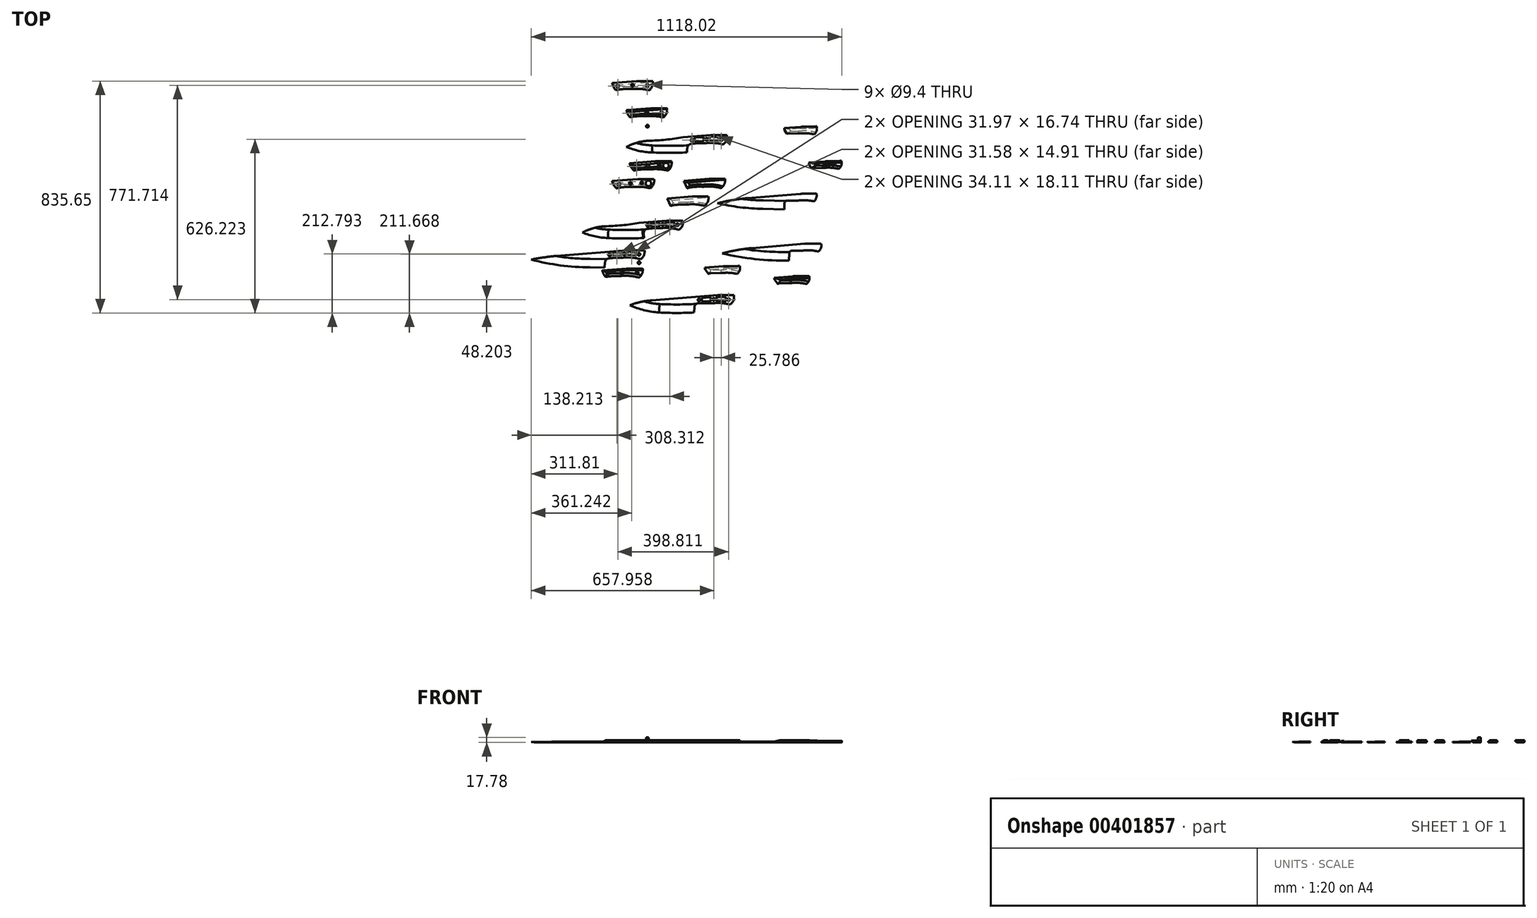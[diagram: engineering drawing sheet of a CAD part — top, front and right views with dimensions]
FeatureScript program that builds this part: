
annotation { "Feature Type Name" : "Feature", "Feature Type Description" : "" }
export const myFeature = defineFeature(function(context is Context, id is Id, definition is map)
    precondition{}
    {
        {
            var Q0;
            Q0=qCreatedBy(makeId("Top.planeOp"),FACE);
            var sketch = newSketch(context, id + "F0", { "sketchPlane" : qUnion([Q0])});
            skArc(sketch, "E0", {"start": v(-169.03, 335.4) * mm, "mid": v(-124.02, 321.28) * mm, "end": v(-77.2, 315.47) * mm});
            skArc(sketch, "E1", {"start": v(-77.2, 315.47) * mm, "mid": v(-14.27, 313.87) * mm, "end": v(48.66, 315.47) * mm});
            skArc(sketch, "E2", {"start": v(-90.69, 357.62) * mm, "mid": v(-131.02, 350.63) * mm, "end": v(-169.03, 335.4) * mm});
            skArc(sketch, "E3", {"start": v(-90.69, 357.62) * mm, "mid": v(-27.7, 361.34) * mm, "end": v(34.82, 369.92) * mm});
            skLineSegment(sketch, "E4", {"start": v(34.82, 369.92) * mm, "end": v(134.22, 377.8) * mm});
            skLineSegment(sketch, "E5", {"start": v(134.22, 377.8) * mm, "end": v(192.48, 377.8) * mm});
            skArc(sketch, "E6", {"start": v(179.14, 344.37) * mm, "mid": v(146.96, 349.5) * mm, "end": v(114.37, 348.8) * mm});
            skArc(sketch, "E7", {"start": v(179.14, 344.37) * mm, "mid": v(190.65, 359.16) * mm, "end": v(192.48, 377.8) * mm});
            skArc(sketch, "E8", {"start": v(114.37, 348.8) * mm, "mid": v(89.47, 349.08) * mm, "end": v(64.72, 346.26) * mm});
            skLineSegment(sketch, "E9", {"start": v(48.66, 315.47) * mm, "end": v(50.15, 331.6) * mm});
            skArc(sketch, "E10", {"start": v(64.72, 346.26) * mm, "mid": v(54.8, 341.55) * mm, "end": v(50.15, 331.6) * mm});
            skCircle(sketch, "E11", {"center": v(66.88, 359.7) * mm, "radius": 4.7 * mm});
            skCircle(sketch, "E12", {"center": v(173.1, 362.07) * mm, "radius": 4.7 * mm});
            skCircle(sketch, "E13", {"center": v(119.8, 363) * mm, "radius": 4.7 * mm});
            skArc(sketch, "E14", {"start": v(159.01, 354.25) * mm, "mid": v(146.32, 355.71) * mm, "end": v(133.55, 356) * mm});
            skArc(sketch, "E15", {"start": v(159.79, 371.2) * mm, "mid": v(146.02, 372.18) * mm, "end": v(132.22, 372.3) * mm});
            skArc(sketch, "E16", {"start": v(105.5, 355.53) * mm, "mid": v(93.56, 355.5) * mm, "end": v(81.67, 354.5) * mm});
            skLineSegment(sketch, "E17", {"start": v(79.5, 368.63) * mm, "end": v(104.68, 370.41) * mm});
            skArc(sketch, "E18", {"start": v(79.5, 368.63) * mm, "mid": v(77.02, 367.18) * mm, "end": v(76.66, 364.33) * mm});
            skArc(sketch, "E19", {"start": v(77.57, 358.02) * mm, "mid": v(78.79, 355.3) * mm, "end": v(81.67, 354.5) * mm});
            skArc(sketch, "E20", {"start": v(77.57, 358.02) * mm, "mid": v(77.6, 361.24) * mm, "end": v(76.66, 364.33) * mm});
            skArc(sketch, "E21", {"start": v(109.33, 365.54) * mm, "mid": v(108.15, 369.07) * mm, "end": v(104.68, 370.41) * mm});
            skArc(sketch, "E22", {"start": v(105.5, 355.53) * mm, "mid": v(108.55, 357.08) * mm, "end": v(109.33, 360.42) * mm});
            skArc(sketch, "E23", {"start": v(109.33, 365.54) * mm, "mid": v(109.01, 362.98) * mm, "end": v(109.33, 360.42) * mm});
            skArc(sketch, "E24", {"start": v(132.22, 372.3) * mm, "mid": v(129.65, 370.86) * mm, "end": v(129.4, 367.91) * mm});
            skArc(sketch, "E25", {"start": v(130.2, 360.09) * mm, "mid": v(130.86, 357.21) * mm, "end": v(133.55, 356) * mm});
            skArc(sketch, "E26", {"start": v(130.2, 360.09) * mm, "mid": v(130.55, 364.08) * mm, "end": v(129.4, 367.91) * mm});
            skArc(sketch, "E27", {"start": v(163.12, 366.2) * mm, "mid": v(162.63, 369.48) * mm, "end": v(159.79, 371.2) * mm});
            skArc(sketch, "E28", {"start": v(159.01, 354.25) * mm, "mid": v(162.07, 355.4) * mm, "end": v(162.9, 358.55) * mm});
            skArc(sketch, "E29", {"start": v(163.12, 366.2) * mm, "mid": v(162.3, 362.4) * mm, "end": v(162.9, 358.55) * mm});
            skSolve(sketch);
        }
        {
            var Q0;
            Q0=makeQuery(id+"F0.imprint","IMPRINT",FACE,{"disambiguationData":[TD([[makeQuery(id+"F0.imprint","IMPRINT",EDGE,{"derivedFrom":sQuery(id+"F0.wireOp",EDGE,"E0")}),1.0]])]});
            extrude(context, id + "F1", {"entities" : qUnion([Q0]), "depth" : 2.54 * mm});
        }
        {
            var Q0;
            Q0=qCreatedBy(makeId("Top.planeOp"),FACE);
            var sketch = newSketch(context, id + "F2", { "sketchPlane" : qUnion([Q0])});
            skArc(sketch, "E30", {"start": v(-175.57, 178.14) * mm, "mid": v(-130.56, 164.01) * mm, "end": v(-83.74, 158.2) * mm});
            skArc(sketch, "E31", {"start": v(-83.74, 158.2) * mm, "mid": v(-20.8, 156.6) * mm, "end": v(42.12, 158.2) * mm});
            skArc(sketch, "E32", {"start": v(-97.23, 200.35) * mm, "mid": v(-137.56, 193.36) * mm, "end": v(-175.57, 178.14) * mm});
            skArc(sketch, "E33", {"start": v(-97.23, 200.35) * mm, "mid": v(-34.23, 204.08) * mm, "end": v(28.29, 212.65) * mm});
            skLineSegment(sketch, "E34", {"start": v(28.29, 212.65) * mm, "end": v(127.68, 220.54) * mm});
            skLineSegment(sketch, "E35", {"start": v(127.68, 220.54) * mm, "end": v(185.94, 220.54) * mm});
            skArc(sketch, "E36", {"start": v(172.6, 187.1) * mm, "mid": v(140.42, 192.24) * mm, "end": v(107.83, 191.52) * mm});
            skArc(sketch, "E37", {"start": v(172.6, 187.1) * mm, "mid": v(184.11, 201.89) * mm, "end": v(185.94, 220.54) * mm});
            skArc(sketch, "E38", {"start": v(107.83, 191.52) * mm, "mid": v(82.93, 191.81) * mm, "end": v(58.18, 189) * mm});
            skLineSegment(sketch, "E39", {"start": v(42.12, 158.2) * mm, "end": v(43.61, 174.34) * mm});
            skArc(sketch, "E40", {"start": v(58.18, 189) * mm, "mid": v(48.26, 184.28) * mm, "end": v(43.61, 174.34) * mm});
            skLineSegment(sketch, "E41", {"start": v(37.58, 213.39) * mm, "end": v(50.38, 186.08) * mm});
            skLineSegment(sketch, "E42", {"start": v(58.18, 189) * mm, "end": v(49.42, 188.13) * mm});
            skSolve(sketch);
        }
        {
            var Q0;
            {var subQ0=sQuery(id+"F2.wireOp",EDGE,"E35");Q0=makeQuery(id+"F2.imprint","IMPRINT",FACE,{"disambiguationData":[TD([[makeQuery(id+"F2.imprint","IMPRINT",EDGE,{"derivedFrom":subQ0}),-1.0]])]});}
            var Q1;
            {var subQ0=sQuery(id+"F2.wireOp",EDGE,"E42");Q1=makeQuery(id+"F2.imprint","IMPRINT",FACE,{"disambiguationData":[TD([[makeQuery(id+"F2.imprint","IMPRINT",EDGE,{"derivedFrom":subQ0}),1.0]])]});}
            extrude(context, id + "F3", {"entities" : qUnion([Q0, Q1]), "depth" : 7.62 * mm, "offsetDistance" : 25.4 * mm});
        }
        {
            var Q0;
            Q0=makeQuery(id+"F3.opExtrude","CAP_EDGE",EDGE,{"disambiguationData":[OSD([sQuery(id+"F2.wireOp",EDGE,"E41")])],"isStart":false});
            chamfer(context, id + "F4", {"entities" : qUnion([Q0]), "chamferType" : ChamferType.TWO_OFFSETS, "width1" : 12.7 * mm, "oppositeDirection" : false, "width2" : 5.08 * mm, "tangentPropagation" : true});
        }
        {
            var Q0;
            Q0=makeQuery(id+"F1.opExtrude","CAP_EDGE",EDGE,{"disambiguationData":[OSD([sQuery(id+"F0.wireOp",EDGE,"E1")])],"isStart":false});
            var Q1;
            Q1=makeQuery(id+"F1.opExtrude","CAP_EDGE",EDGE,{"disambiguationData":[OSD([sQuery(id+"F0.wireOp",EDGE,"E0")])],"isStart":false});
            var Q2;
            Q2=makeQuery(id+"F1.opExtrude","CAP_EDGE",EDGE,{"disambiguationData":[OSD([sQuery(id+"F0.wireOp",EDGE,"E1")])],"isStart":true});
            var Q3;
            Q3=makeQuery(id+"F1.opExtrude","CAP_EDGE",EDGE,{"disambiguationData":[OSD([sQuery(id+"F0.wireOp",EDGE,"E0")])],"isStart":true});
            chamfer(context, id + "F5", {"entities" : qUnion([Q0, Q1, Q2, Q3]), "chamferType" : ChamferType.TWO_OFFSETS, "width1" : 25.4 * mm, "oppositeDirection" : false, "width2" : 1.02 * mm, "tangentPropagation" : true});
        }
        {
            var Q0;
            Q0=qCreatedBy(makeId("Top.planeOp"),FACE);
            var sketch = newSketch(context, id + "F6", { "sketchPlane" : qUnion([Q0])});
            skArc(sketch, "E43", {"start": v(-235.43, 114.12) * mm, "mid": v(-190.43, 100) * mm, "end": v(-143.61, 94.19) * mm});
            skArc(sketch, "E44", {"start": v(-143.61, 94.19) * mm, "mid": v(-80.68, 92.58) * mm, "end": v(-17.74, 94.19) * mm});
            skArc(sketch, "E45", {"start": v(-157.1, 136.34) * mm, "mid": v(-197.43, 129.34) * mm, "end": v(-235.43, 114.12) * mm});
            skArc(sketch, "E46", {"start": v(-157.1, 136.34) * mm, "mid": v(-94.1, 140.06) * mm, "end": v(-31.58, 148.64) * mm});
            skLineSegment(sketch, "E47", {"start": v(-31.58, 148.64) * mm, "end": v(67.8, 156.52) * mm});
            skLineSegment(sketch, "E48", {"start": v(67.8, 156.52) * mm, "end": v(126.07, 156.52) * mm});
            skArc(sketch, "E49", {"start": v(112.74, 123.09) * mm, "mid": v(80.55, 128.22) * mm, "end": v(47.97, 127.5) * mm});
            skArc(sketch, "E50", {"start": v(112.74, 123.09) * mm, "mid": v(124.24, 137.87) * mm, "end": v(126.07, 156.52) * mm});
            skArc(sketch, "E51", {"start": v(47.97, 127.5) * mm, "mid": v(23.06, 127.8) * mm, "end": v(-1.69, 124.98) * mm});
            skLineSegment(sketch, "E52", {"start": v(-17.74, 94.19) * mm, "end": v(-16.26, 110.32) * mm});
            skArc(sketch, "E53", {"start": v(-1.69, 124.98) * mm, "mid": v(-11.6, 120.27) * mm, "end": v(-16.26, 110.32) * mm});
            skLineSegment(sketch, "E54", {"start": v(-22.28, 149.37) * mm, "end": v(-9.49, 122.07) * mm});
            skLineSegment(sketch, "E55", {"start": v(-1.69, 124.98) * mm, "end": v(-10.45, 124.12) * mm});
            skSolve(sketch);
        }
        {
            var Q0;
            {var subQ0=sQuery(id+"F6.wireOp",EDGE,"E48");Q0=makeQuery(id+"F6.imprint","IMPRINT",FACE,{"disambiguationData":[TD([[makeQuery(id+"F6.imprint","IMPRINT",EDGE,{"derivedFrom":subQ0}),-1.0]])]});}
            var Q1;
            {var subQ0=sQuery(id+"F6.wireOp",EDGE,"E55");Q1=makeQuery(id+"F6.imprint","IMPRINT",FACE,{"disambiguationData":[TD([[makeQuery(id+"F6.imprint","IMPRINT",EDGE,{"derivedFrom":subQ0}),1.0]])]});}
            extrude(context, id + "F7", {"entities" : qUnion([Q0, Q1]), "depth" : 7.62 * mm, "offsetDistance" : 25.4 * mm});
        }
        {
            var Q0;
            Q0=makeQuery(id+"F7.opExtrude","CAP_EDGE",EDGE,{"disambiguationData":[OSD([sQuery(id+"F6.wireOp",EDGE,"E54")])],"isStart":true});
            chamfer(context, id + "F8", {"entities" : qUnion([Q0]), "chamferType" : ChamferType.TWO_OFFSETS, "width1" : 5.08 * mm, "oppositeDirection" : false, "width2" : 12.7 * mm, "tangentPropagation" : true});
        }
        {
            var Q0;
            Q0=makeQuery(id+"F7.opExtrude","CAP_EDGE",EDGE,{"disambiguationData":[OSD([sQuery(id+"F6.wireOp",EDGE,"E51")])],"isStart":true});
            var Q1;
            Q1=makeQuery(id+"F7.opExtrude","CAP_EDGE",EDGE,{"disambiguationData":[OSD([sQuery(id+"F6.wireOp",EDGE,"E47")])],"isStart":true});
            chamfer(context, id + "F9", {"entities" : qUnion([Q0, Q1]), "chamferType" : ChamferType.TWO_OFFSETS, "width1" : 7.62 * mm, "oppositeDirection" : false, "width2" : 5.08 * mm, "tangentPropagation" : true});
        }
        {
            var Q0;
            Q0=makeQuery(id+"F3.opExtrude","CAP_EDGE",EDGE,{"disambiguationData":[OSD([sQuery(id+"F2.wireOp",EDGE,"E34")])],"isStart":false});
            var Q1;
            Q1=makeQuery(id+"F3.opExtrude","CAP_EDGE",EDGE,{"disambiguationData":[OSD([sQuery(id+"F2.wireOp",EDGE,"E38")])],"isStart":false});
            chamfer(context, id + "F10", {"entities" : qUnion([Q0, Q1]), "chamferType" : ChamferType.TWO_OFFSETS, "width1" : 5.08 * mm, "oppositeDirection" : false, "width2" : 7.62 * mm, "tangentPropagation" : true});
        }
        {
            var Q0;
            Q0=makeQuery(id+"F3.opExtrude","CAP_EDGE",EDGE,{"disambiguationData":[OSD([sQuery(id+"F2.wireOp",EDGE,"E36")])],"isStart":false});
            var Q1;
            Q1=makeQuery(id+"F10.opChamfer","BLEND_EDGE",EDGE,{"blendedFrom":[makeQuery(id+"F3.opExtrude","CAP_EDGE",EDGE,{"disambiguationData":[OSD([sQuery(id+"F2.wireOp",EDGE,"E34")])],"isStart":false}),makeQuery(id+"F3.opExtrude","SWEPT_FACE",FACE,{"disambiguationData":[OSD([sQuery(id+"F2.wireOp",EDGE,"E35")])]})],"blendedInto":[makeQuery(id+"F3.opExtrude","SWEPT_FACE",FACE,{"disambiguationData":[OSD([sQuery(id+"F2.wireOp",EDGE,"E35")])]})]});
            chamfer(context, id + "F11", {"entities" : qUnion([Q0, Q1]), "chamferType" : ChamferType.TWO_OFFSETS, "width1" : 5.08 * mm, "oppositeDirection" : false, "width2" : 7.62 * mm, "tangentPropagation" : true});
        }
        {
            var Q0;
            Q0=makeQuery(id+"F7.opExtrude","CAP_EDGE",EDGE,{"disambiguationData":[OSD([sQuery(id+"F6.wireOp",EDGE,"E49")])],"isStart":true});
            chamfer(context, id + "F12", {"entities" : qUnion([Q0]), "chamferType" : ChamferType.TWO_OFFSETS, "width1" : 7.62 * mm, "oppositeDirection" : false, "width2" : 5.08 * mm, "tangentPropagation" : true});
        }
        {
            var Q0;
            Q0=qCreatedBy(makeId("Top.planeOp"),FACE);
            var sketch = newSketch(context, id + "F13", { "sketchPlane" : qUnion([Q0])});
            skArc(sketch, "E56", {"start": v(-367.85, 241) * mm, "mid": v(-322.84, 226.88) * mm, "end": v(-276.03, 221.07) * mm});
            skArc(sketch, "E57", {"start": v(-276.03, 221.07) * mm, "mid": v(-213.1, 219.46) * mm, "end": v(-150.16, 221.07) * mm});
            skArc(sketch, "E58", {"start": v(-289.51, 263.21) * mm, "mid": v(-329.85, 256.22) * mm, "end": v(-367.85, 241) * mm});
            skArc(sketch, "E59", {"start": v(-289.51, 263.21) * mm, "mid": v(-226.52, 266.94) * mm, "end": v(-164, 275.52) * mm});
            skLineSegment(sketch, "E60", {"start": v(-164, 275.52) * mm, "end": v(-64.6, 283.4) * mm});
            skLineSegment(sketch, "E61", {"start": v(-64.6, 283.4) * mm, "end": v(-6.35, 283.4) * mm});
            skArc(sketch, "E62", {"start": v(-19.68, 249.97) * mm, "mid": v(-51.87, 255.1) * mm, "end": v(-84.45, 254.39) * mm});
            skArc(sketch, "E63", {"start": v(-19.68, 249.97) * mm, "mid": v(-8.17, 264.75) * mm, "end": v(-6.35, 283.4) * mm});
            skArc(sketch, "E64", {"start": v(-84.45, 254.39) * mm, "mid": v(-109.36, 254.68) * mm, "end": v(-134.1, 251.86) * mm});
            skLineSegment(sketch, "E65", {"start": v(-150.16, 221.07) * mm, "end": v(-148.67, 237.2) * mm});
            skArc(sketch, "E66", {"start": v(-134.1, 251.86) * mm, "mid": v(-144.02, 247.15) * mm, "end": v(-148.67, 237.2) * mm});
            skCircle(sketch, "E67", {"center": v(-26.4, 268.03) * mm, "radius": 10.1 * mm});
            skCircle(sketch, "E68", {"center": v(-131.94, 265.3) * mm, "radius": 4.7 * mm});
            skCircle(sketch, "E69", {"center": v(-91.41, 267.64) * mm, "radius": 4.71 * mm});
            skCircle(sketch, "E70", {"center": v(-50.47, 269.22) * mm, "radius": 4.7 * mm});
            skLineSegment(sketch, "E71", {"start": v(-119.06, 273.98) * mm, "end": v(-106.19, 274.89) * mm});
            skLineSegment(sketch, "E72", {"start": v(-117.66, 260.1) * mm, "end": v(-105.57, 260.91) * mm});
            skLineSegment(sketch, "E73", {"start": v(-78.86, 277.2) * mm, "end": v(-63.77, 277.87) * mm});
            skLineSegment(sketch, "E74", {"start": v(-78.15, 261.02) * mm, "end": v(-63.57, 261.71) * mm});
            skArc(sketch, "E75", {"start": v(-78.86, 277.2) * mm, "mid": v(-81.33, 275.81) * mm, "end": v(-81.71, 273) * mm});
            skArc(sketch, "E76", {"start": v(-63.57, 261.71) * mm, "mid": v(-61.18, 263.02) * mm, "end": v(-60.72, 265.7) * mm});
            skArc(sketch, "E77", {"start": v(-60.38, 273.61) * mm, "mid": v(-61, 276.6) * mm, "end": v(-63.77, 277.87) * mm});
            skArc(sketch, "E78", {"start": v(-80.88, 265.13) * mm, "mid": v(-80.68, 262.3) * mm, "end": v(-78.15, 261.02) * mm});
            skArc(sketch, "E79", {"start": v(-80.88, 265.13) * mm, "mid": v(-80.55, 269.14) * mm, "end": v(-81.71, 273) * mm});
            skArc(sketch, "E80", {"start": v(-60.38, 273.61) * mm, "mid": v(-61.3, 269.69) * mm, "end": v(-60.72, 265.7) * mm});
            skArc(sketch, "E81", {"start": v(-119.06, 273.98) * mm, "mid": v(-121.72, 272.33) * mm, "end": v(-121.88, 269.2) * mm});
            skArc(sketch, "E82", {"start": v(-121.27, 263.7) * mm, "mid": v(-120.28, 261.09) * mm, "end": v(-117.66, 260.1) * mm});
            skArc(sketch, "E83", {"start": v(-101.85, 270.28) * mm, "mid": v(-102.93, 273.61) * mm, "end": v(-106.19, 274.89) * mm});
            skArc(sketch, "E84", {"start": v(-105.57, 260.91) * mm, "mid": v(-102.59, 262.6) * mm, "end": v(-102.06, 266) * mm});
            skArc(sketch, "E85", {"start": v(-101.85, 270.28) * mm, "mid": v(-102.21, 268.15) * mm, "end": v(-102.06, 266) * mm});
            skArc(sketch, "E86", {"start": v(-121.27, 263.7) * mm, "mid": v(-121.22, 266.5) * mm, "end": v(-121.88, 269.2) * mm});
            skArc(sketch, "E87", {"start": v(-157.02, 276.07) * mm, "mid": v(-151.1, 261.47) * mm, "end": v(-140.43, 249.87) * mm});
            skSolve(sketch);
        }
        {
            var Q0;
            {var subQ0=sQuery(id+"F13.wireOp",EDGE,"E61");Q0=makeQuery(id+"F13.imprint","IMPRINT",FACE,{"disambiguationData":[TD([[makeQuery(id+"F13.imprint","IMPRINT",EDGE,{"derivedFrom":subQ0}),-1.0]])]});}
            var Q1;
            Q1=makeQuery(id+"F13.imprint","IMPRINT",FACE,{"disambiguationData":[TD([[makeQuery(id+"F13.imprint","IMPRINT",EDGE,{"derivedFrom":sQuery(id+"F13.wireOp",EDGE,"E71")}),-1.0]])]});
            var Q2;
            Q2=makeQuery(id+"F13.imprint","IMPRINT",FACE,{"disambiguationData":[TD([[makeQuery(id+"F13.imprint","IMPRINT",EDGE,{"derivedFrom":sQuery(id+"F13.wireOp",EDGE,"E73")}),-1.0]])]});
            extrude(context, id + "F14", {"entities" : qUnion([Q0, Q1, Q2]), "depth" : 7.62 * mm, "offsetDistance" : 25.4 * mm});
        }
        {
            var Q0;
            Q0=qCreatedBy(makeId("Top.planeOp"),FACE);
            var sketch = newSketch(context, id + "F15", { "sketchPlane" : qUnion([Q0])});
            skArc(sketch, "E88", {"start": v(-431.18, 177.25) * mm, "mid": v(-386.18, 163.13) * mm, "end": v(-339.36, 157.32) * mm});
            skArc(sketch, "E89", {"start": v(-339.36, 157.32) * mm, "mid": v(-276.43, 155.71) * mm, "end": v(-213.5, 157.32) * mm});
            skArc(sketch, "E90", {"start": v(-352.84, 199.46) * mm, "mid": v(-393.18, 192.47) * mm, "end": v(-431.18, 177.25) * mm});
            skArc(sketch, "E91", {"start": v(-352.84, 199.46) * mm, "mid": v(-289.85, 203.19) * mm, "end": v(-227.33, 211.77) * mm});
            skLineSegment(sketch, "E92", {"start": v(-227.33, 211.77) * mm, "end": v(-127.94, 219.65) * mm});
            skLineSegment(sketch, "E93", {"start": v(-127.94, 219.65) * mm, "end": v(-69.68, 219.65) * mm});
            skArc(sketch, "E94", {"start": v(-83.01, 186.22) * mm, "mid": v(-115.2, 191.35) * mm, "end": v(-147.78, 190.64) * mm});
            skArc(sketch, "E95", {"start": v(-83.01, 186.22) * mm, "mid": v(-71.5, 201) * mm, "end": v(-69.68, 219.65) * mm});
            skArc(sketch, "E96", {"start": v(-147.78, 190.64) * mm, "mid": v(-172.7, 190.93) * mm, "end": v(-197.44, 188.1) * mm});
            skLineSegment(sketch, "E97", {"start": v(-213.5, 157.32) * mm, "end": v(-212, 173.45) * mm});
            skArc(sketch, "E98", {"start": v(-197.44, 188.1) * mm, "mid": v(-207.36, 183.4) * mm, "end": v(-212, 173.45) * mm});
            skCircle(sketch, "E99", {"center": v(-89.73, 204.28) * mm, "radius": 10.1 * mm});
            skCircle(sketch, "E100", {"center": v(-195.27, 201.54) * mm, "radius": 4.7 * mm});
            skCircle(sketch, "E101", {"center": v(-154.75, 203.9) * mm, "radius": 4.71 * mm});
            skCircle(sketch, "E102", {"center": v(-113.8, 205.47) * mm, "radius": 4.7 * mm});
            skLineSegment(sketch, "E103", {"start": v(-182.4, 210.23) * mm, "end": v(-169.52, 211.14) * mm});
            skLineSegment(sketch, "E104", {"start": v(-181, 196.36) * mm, "end": v(-168.9, 197.16) * mm});
            skLineSegment(sketch, "E105", {"start": v(-142.19, 213.45) * mm, "end": v(-127.1, 214.12) * mm});
            skLineSegment(sketch, "E106", {"start": v(-141.49, 197.27) * mm, "end": v(-126.9, 197.97) * mm});
            skArc(sketch, "E107", {"start": v(-142.19, 213.45) * mm, "mid": v(-144.67, 212.07) * mm, "end": v(-145.05, 209.25) * mm});
            skArc(sketch, "E108", {"start": v(-126.9, 197.97) * mm, "mid": v(-124.52, 199.27) * mm, "end": v(-124.06, 201.95) * mm});
            skArc(sketch, "E109", {"start": v(-123.72, 209.86) * mm, "mid": v(-124.33, 212.85) * mm, "end": v(-127.1, 214.12) * mm});
            skArc(sketch, "E110", {"start": v(-144.2, 201.38) * mm, "mid": v(-144.02, 198.55) * mm, "end": v(-141.49, 197.27) * mm});
            skArc(sketch, "E111", {"start": v(-144.2, 201.38) * mm, "mid": v(-143.89, 205.4) * mm, "end": v(-145.05, 209.25) * mm});
            skArc(sketch, "E112", {"start": v(-123.72, 209.86) * mm, "mid": v(-124.64, 205.94) * mm, "end": v(-124.06, 201.95) * mm});
            skArc(sketch, "E113", {"start": v(-182.4, 210.23) * mm, "mid": v(-185.06, 208.58) * mm, "end": v(-185.21, 205.46) * mm});
            skArc(sketch, "E114", {"start": v(-184.6, 199.95) * mm, "mid": v(-183.61, 197.34) * mm, "end": v(-181, 196.36) * mm});
            skArc(sketch, "E115", {"start": v(-165.19, 206.53) * mm, "mid": v(-166.26, 209.86) * mm, "end": v(-169.52, 211.14) * mm});
            skArc(sketch, "E116", {"start": v(-168.9, 197.16) * mm, "mid": v(-165.92, 198.86) * mm, "end": v(-165.39, 202.25) * mm});
            skArc(sketch, "E117", {"start": v(-165.19, 206.53) * mm, "mid": v(-165.55, 204.4) * mm, "end": v(-165.39, 202.25) * mm});
            skArc(sketch, "E118", {"start": v(-184.6, 199.95) * mm, "mid": v(-184.55, 202.74) * mm, "end": v(-185.21, 205.46) * mm});
            skArc(sketch, "E119", {"start": v(-220.36, 212.32) * mm, "mid": v(-214.43, 197.72) * mm, "end": v(-203.77, 186.12) * mm});
            skSolve(sketch);
        }
        {
            var Q0;
            {var subQ0=sQuery(id+"F15.wireOp",EDGE,"E93");Q0=makeQuery(id+"F15.imprint","IMPRINT",FACE,{"disambiguationData":[TD([[makeQuery(id+"F15.imprint","IMPRINT",EDGE,{"derivedFrom":subQ0}),-1.0]])]});}
            var Q1;
            Q1=makeQuery(id+"F15.imprint","IMPRINT",FACE,{"disambiguationData":[TD([[makeQuery(id+"F15.imprint","IMPRINT",EDGE,{"derivedFrom":sQuery(id+"F15.wireOp",EDGE,"E103")}),-1.0]])]});
            var Q2;
            Q2=makeQuery(id+"F15.imprint","IMPRINT",FACE,{"disambiguationData":[TD([[makeQuery(id+"F15.imprint","IMPRINT",EDGE,{"derivedFrom":sQuery(id+"F15.wireOp",EDGE,"E105")}),-1.0]])]});
            extrude(context, id + "F16", {"entities" : qUnion([Q0, Q1, Q2]), "depth" : 7.62 * mm, "offsetDistance" : 25.4 * mm});
        }
        {
            var Q0;
            Q0=makeQuery(id+"F14.opExtrude","CAP_EDGE",EDGE,{"disambiguationData":[OSD([sQuery(id+"F13.wireOp",EDGE,"E87")])],"isStart":false});
            var Q1;
            Q1=makeQuery(id+"F14.opExtrude","CAP_EDGE",EDGE,{"disambiguationData":[OSD([sQuery(id+"F13.wireOp",EDGE,"E64")])],"isStart":false});
            var Q2;
            Q2=makeQuery(id+"F14.opExtrude","CAP_EDGE",EDGE,{"disambiguationData":[OSD([sQuery(id+"F13.wireOp",EDGE,"E60")])],"isStart":false});
            var Q3;
            Q3=makeQuery(id+"F14.opExtrude","CAP_EDGE",EDGE,{"disambiguationData":[OSD([sQuery(id+"F13.wireOp",EDGE,"E62")])],"isStart":false});
            chamfer(context, id + "F17", {"entities" : qUnion([Q0, Q1, Q2, Q3]), "chamferType" : ChamferType.TWO_OFFSETS, "width1" : 7.62 * mm, "oppositeDirection" : false, "width2" : 5.08 * mm, "tangentPropagation" : true});
        }
        {
            var Q0;
            Q0=makeQuery(id+"F16.opExtrude","CAP_EDGE",EDGE,{"disambiguationData":[OSD([sQuery(id+"F15.wireOp",EDGE,"E119")])],"isStart":true});
            var Q1;
            Q1=makeQuery(id+"F16.opExtrude","CAP_EDGE",EDGE,{"disambiguationData":[OSD([sQuery(id+"F15.wireOp",EDGE,"E92")])],"isStart":true});
            var Q2;
            Q2=makeQuery(id+"F16.opExtrude","CAP_EDGE",EDGE,{"disambiguationData":[OSD([sQuery(id+"F15.wireOp",EDGE,"E96")])],"isStart":true});
            var Q3;
            Q3=makeQuery(id+"F16.opExtrude","CAP_EDGE",EDGE,{"disambiguationData":[OSD([sQuery(id+"F15.wireOp",EDGE,"E94")])],"isStart":true});
            chamfer(context, id + "F18", {"entities" : qUnion([Q0, Q1, Q2, Q3]), "chamferType" : ChamferType.TWO_OFFSETS, "width1" : 5.08 * mm, "oppositeDirection" : false, "width2" : 7.62 * mm, "tangentPropagation" : true});
        }
        {
            var Q0;
            Q0=qCreatedBy(makeId("Top.planeOp"),FACE);
            var sketch = newSketch(context, id + "F19", { "sketchPlane" : qUnion([Q0])});
            skArc(sketch, "E120", {"start": v(-384.45, 432.43) * mm, "mid": v(-339.44, 418.3) * mm, "end": v(-292.63, 412.5) * mm});
            skArc(sketch, "E121", {"start": v(-292.63, 412.5) * mm, "mid": v(-229.7, 410.89) * mm, "end": v(-166.76, 412.5) * mm});
            skArc(sketch, "E122", {"start": v(-306.11, 454.64) * mm, "mid": v(-346.45, 447.65) * mm, "end": v(-384.45, 432.43) * mm});
            skArc(sketch, "E123", {"start": v(-306.11, 454.64) * mm, "mid": v(-243.12, 458.37) * mm, "end": v(-180.6, 466.94) * mm});
            skLineSegment(sketch, "E124", {"start": v(-180.6, 466.94) * mm, "end": v(-81.21, 474.83) * mm});
            skLineSegment(sketch, "E125", {"start": v(-81.21, 474.83) * mm, "end": v(-22.95, 474.83) * mm});
            skArc(sketch, "E126", {"start": v(-36.28, 441.4) * mm, "mid": v(-68.47, 446.53) * mm, "end": v(-101.05, 445.81) * mm});
            skArc(sketch, "E127", {"start": v(-36.28, 441.4) * mm, "mid": v(-24.78, 456.18) * mm, "end": v(-22.95, 474.83) * mm});
            skArc(sketch, "E128", {"start": v(-101.05, 445.81) * mm, "mid": v(-125.96, 446.1) * mm, "end": v(-150.7, 443.29) * mm});
            skLineSegment(sketch, "E129", {"start": v(-166.76, 412.5) * mm, "end": v(-165.27, 428.63) * mm});
            skArc(sketch, "E130", {"start": v(-150.7, 443.29) * mm, "mid": v(-160.63, 438.58) * mm, "end": v(-165.27, 428.63) * mm});
            skCircle(sketch, "E131", {"center": v(-148.54, 456.72) * mm, "radius": 4.7 * mm});
            skCircle(sketch, "E132", {"center": v(-42.33, 459.1) * mm, "radius": 4.7 * mm});
            skCircle(sketch, "E133", {"center": v(-95.62, 460.01) * mm, "radius": 4.7 * mm});
            skArc(sketch, "E134", {"start": v(-56.41, 451.28) * mm, "mid": v(-69.1, 452.74) * mm, "end": v(-81.87, 453.02) * mm});
            skArc(sketch, "E135", {"start": v(-55.64, 468.21) * mm, "mid": v(-69.4, 469.2) * mm, "end": v(-83.2, 469.33) * mm});
            skArc(sketch, "E136", {"start": v(-109.93, 452.55) * mm, "mid": v(-121.87, 452.53) * mm, "end": v(-133.76, 451.53) * mm});
            skLineSegment(sketch, "E137", {"start": v(-135.92, 465.66) * mm, "end": v(-110.74, 467.44) * mm});
            skArc(sketch, "E138", {"start": v(-135.92, 465.66) * mm, "mid": v(-138.4, 464.2) * mm, "end": v(-138.77, 461.35) * mm});
            skArc(sketch, "E139", {"start": v(-137.86, 455.05) * mm, "mid": v(-136.64, 452.32) * mm, "end": v(-133.76, 451.53) * mm});
            skArc(sketch, "E140", {"start": v(-137.86, 455.05) * mm, "mid": v(-137.83, 458.27) * mm, "end": v(-138.77, 461.35) * mm});
            skArc(sketch, "E141", {"start": v(-106.1, 462.56) * mm, "mid": v(-107.27, 466.1) * mm, "end": v(-110.74, 467.44) * mm});
            skArc(sketch, "E142", {"start": v(-109.93, 452.55) * mm, "mid": v(-106.87, 454.1) * mm, "end": v(-106.1, 457.44) * mm});
            skArc(sketch, "E143", {"start": v(-106.1, 462.56) * mm, "mid": v(-106.41, 460) * mm, "end": v(-106.1, 457.44) * mm});
            skArc(sketch, "E144", {"start": v(-83.2, 469.33) * mm, "mid": v(-85.78, 467.88) * mm, "end": v(-86.02, 464.94) * mm});
            skArc(sketch, "E145", {"start": v(-85.23, 457.11) * mm, "mid": v(-84.57, 454.23) * mm, "end": v(-81.87, 453.02) * mm});
            skArc(sketch, "E146", {"start": v(-85.23, 457.11) * mm, "mid": v(-84.87, 461.1) * mm, "end": v(-86.02, 464.94) * mm});
            skArc(sketch, "E147", {"start": v(-52.3, 463.21) * mm, "mid": v(-52.8, 466.5) * mm, "end": v(-55.64, 468.21) * mm});
            skArc(sketch, "E148", {"start": v(-56.41, 451.28) * mm, "mid": v(-53.35, 452.41) * mm, "end": v(-52.53, 455.57) * mm});
            skArc(sketch, "E149", {"start": v(-52.3, 463.21) * mm, "mid": v(-53.13, 459.41) * mm, "end": v(-52.53, 455.57) * mm});
            skArc(sketch, "E150", {"start": v(-168.44, 467.9) * mm, "mid": v(-164.2, 453.87) * mm, "end": v(-155.5, 442.05) * mm});
            skArc(sketch, "E151", {"start": v(-435.84, 530.34) * mm, "mid": v(-390.83, 516.2) * mm, "end": v(-344.02, 510.4) * mm});
            skArc(sketch, "E152", {"start": v(-344.02, 510.4) * mm, "mid": v(-281.08, 508.8) * mm, "end": v(-218.15, 510.4) * mm});
            skArc(sketch, "E153", {"start": v(-357.5, 552.55) * mm, "mid": v(-397.84, 545.55) * mm, "end": v(-435.84, 530.34) * mm});
            skArc(sketch, "E154", {"start": v(-357.5, 552.55) * mm, "mid": v(-294.5, 556.27) * mm, "end": v(-231.99, 564.85) * mm});
            skLineSegment(sketch, "E155", {"start": v(-231.99, 564.85) * mm, "end": v(-132.6, 572.73) * mm});
            skLineSegment(sketch, "E156", {"start": v(-132.6, 572.73) * mm, "end": v(-74.34, 572.73) * mm});
            skArc(sketch, "E157", {"start": v(-87.67, 539.3) * mm, "mid": v(-119.86, 544.43) * mm, "end": v(-152.44, 543.72) * mm});
            skArc(sketch, "E158", {"start": v(-87.67, 539.3) * mm, "mid": v(-76.16, 554.08) * mm, "end": v(-74.34, 572.73) * mm});
            skArc(sketch, "E159", {"start": v(-152.44, 543.72) * mm, "mid": v(-177.35, 544) * mm, "end": v(-202.1, 541.19) * mm});
            skLineSegment(sketch, "E160", {"start": v(-218.15, 510.4) * mm, "end": v(-216.66, 526.53) * mm});
            skArc(sketch, "E161", {"start": v(-202.1, 541.19) * mm, "mid": v(-212.01, 536.48) * mm, "end": v(-216.66, 526.53) * mm});
            skCircle(sketch, "E162", {"center": v(-199.93, 554.63) * mm, "radius": 4.7 * mm});
            skCircle(sketch, "E163", {"center": v(-93.72, 557) * mm, "radius": 4.7 * mm});
            skCircle(sketch, "E164", {"center": v(-147, 557.92) * mm, "radius": 4.7 * mm});
            skArc(sketch, "E165", {"start": v(-107.8, 549.18) * mm, "mid": v(-120.5, 550.64) * mm, "end": v(-133.26, 550.93) * mm});
            skArc(sketch, "E166", {"start": v(-107.03, 566.12) * mm, "mid": v(-120.8, 567.1) * mm, "end": v(-134.6, 567.23) * mm});
            skArc(sketch, "E167", {"start": v(-161.32, 550.45) * mm, "mid": v(-173.26, 550.43) * mm, "end": v(-185.15, 549.43) * mm});
            skLineSegment(sketch, "E168", {"start": v(-187.31, 563.56) * mm, "end": v(-162.13, 565.34) * mm});
            skArc(sketch, "E169", {"start": v(-187.31, 563.56) * mm, "mid": v(-189.8, 562.1) * mm, "end": v(-190.16, 559.25) * mm});
            skArc(sketch, "E170", {"start": v(-189.25, 552.95) * mm, "mid": v(-188.03, 550.23) * mm, "end": v(-185.15, 549.43) * mm});
            skArc(sketch, "E171", {"start": v(-189.25, 552.95) * mm, "mid": v(-189.22, 556.17) * mm, "end": v(-190.16, 559.25) * mm});
            skArc(sketch, "E172", {"start": v(-157.49, 560.46) * mm, "mid": v(-158.66, 564) * mm, "end": v(-162.13, 565.34) * mm});
            skArc(sketch, "E173", {"start": v(-161.32, 550.45) * mm, "mid": v(-158.26, 552) * mm, "end": v(-157.48, 555.34) * mm});
            skArc(sketch, "E174", {"start": v(-157.49, 560.46) * mm, "mid": v(-157.8, 557.9) * mm, "end": v(-157.48, 555.34) * mm});
            skArc(sketch, "E175", {"start": v(-134.6, 567.23) * mm, "mid": v(-137.17, 565.78) * mm, "end": v(-137.4, 562.84) * mm});
            skArc(sketch, "E176", {"start": v(-136.61, 555.01) * mm, "mid": v(-135.95, 552.14) * mm, "end": v(-133.26, 550.93) * mm});
            skArc(sketch, "E177", {"start": v(-136.61, 555.01) * mm, "mid": v(-136.26, 559) * mm, "end": v(-137.4, 562.84) * mm});
            skArc(sketch, "E178", {"start": v(-103.7, 561.12) * mm, "mid": v(-104.18, 564.4) * mm, "end": v(-107.03, 566.12) * mm});
            skArc(sketch, "E179", {"start": v(-107.8, 549.18) * mm, "mid": v(-104.74, 550.32) * mm, "end": v(-103.92, 553.48) * mm});
            skArc(sketch, "E180", {"start": v(-103.7, 561.12) * mm, "mid": v(-104.52, 557.32) * mm, "end": v(-103.92, 553.48) * mm});
            skArc(sketch, "E181", {"start": v(-219.83, 565.81) * mm, "mid": v(-215.58, 551.77) * mm, "end": v(-206.9, 539.96) * mm});
            skCircle(sketch, "E182", {"center": v(-93.23, 409.92) * mm, "radius": 4.7 * mm});
            skSolve(sketch);
        }
        {
            var Q0;
            {var subQ0=sQuery(id+"F19.wireOp",EDGE,"E125");Q0=makeQuery(id+"F19.imprint","IMPRINT",FACE,{"disambiguationData":[TD([[makeQuery(id+"F19.imprint","IMPRINT",EDGE,{"derivedFrom":subQ0}),-1.0]])]});}
            var Q1;
            Q1=makeQuery(id+"F19.imprint","IMPRINT",FACE,{"disambiguationData":[TD([[makeQuery(id+"F19.imprint","IMPRINT",EDGE,{"derivedFrom":sQuery(id+"F19.wireOp",EDGE,"E136")}),-1.0]])]});
            var Q2;
            Q2=makeQuery(id+"F19.imprint","IMPRINT",FACE,{"disambiguationData":[TD([[makeQuery(id+"F19.imprint","IMPRINT",EDGE,{"derivedFrom":sQuery(id+"F19.wireOp",EDGE,"E134")}),-1.0]])]});
            var Q3;
            {var subQ0=sQuery(id+"F19.wireOp",EDGE,"E156");Q3=makeQuery(id+"F19.imprint","IMPRINT",FACE,{"disambiguationData":[TD([[makeQuery(id+"F19.imprint","IMPRINT",EDGE,{"derivedFrom":subQ0}),-1.0]])]});}
            var Q4;
            Q4=makeQuery(id+"F19.imprint","IMPRINT",FACE,{"disambiguationData":[TD([[makeQuery(id+"F19.imprint","IMPRINT",EDGE,{"derivedFrom":sQuery(id+"F19.wireOp",EDGE,"E167")}),-1.0]])]});
            var Q5;
            Q5=makeQuery(id+"F19.imprint","IMPRINT",FACE,{"disambiguationData":[TD([[makeQuery(id+"F19.imprint","IMPRINT",EDGE,{"derivedFrom":sQuery(id+"F19.wireOp",EDGE,"E165")}),-1.0]])]});
            extrude(context, id + "F20", {"entities" : qUnion([Q0, Q1, Q2, Q3, Q4, Q5]), "depth" : 7.62 * mm, "offsetDistance" : 25.4 * mm});
        }
        {
            var Q0;
            Q0=makeQuery(id+"F20.opExtrude","CAP_EDGE",EDGE,{"disambiguationData":[OSD([sQuery(id+"F19.wireOp",EDGE,"E128")])],"isStart":false});
            var Q1;
            Q1=makeQuery(id+"F20.opExtrude","CAP_EDGE",EDGE,{"disambiguationData":[OSD([sQuery(id+"F19.wireOp",EDGE,"E126")])],"isStart":false});
            var Q2;
            Q2=makeQuery(id+"F20.opExtrude","CAP_EDGE",EDGE,{"disambiguationData":[OSD([sQuery(id+"F19.wireOp",EDGE,"E124")])],"isStart":false});
            chamfer(context, id + "F21", {"entities" : qUnion([Q0, Q1, Q2]), "chamferType" : ChamferType.TWO_OFFSETS, "width1" : 5.08 * mm, "oppositeDirection" : false, "width2" : 7.62 * mm, "tangentPropagation" : true});
        }
        {
            var Q0;
            Q0=makeQuery(id+"F20.opExtrude","CAP_EDGE",EDGE,{"disambiguationData":[OSD([sQuery(id+"F19.wireOp",EDGE,"E181")])],"isStart":true});
            var Q1;
            Q1=makeQuery(id+"F20.opExtrude","CAP_EDGE",EDGE,{"disambiguationData":[OSD([sQuery(id+"F19.wireOp",EDGE,"E155")])],"isStart":true});
            var Q2;
            Q2=makeQuery(id+"F20.opExtrude","CAP_EDGE",EDGE,{"disambiguationData":[OSD([sQuery(id+"F19.wireOp",EDGE,"E159")])],"isStart":true});
            var Q3;
            Q3=makeQuery(id+"F20.opExtrude","CAP_EDGE",EDGE,{"disambiguationData":[OSD([sQuery(id+"F19.wireOp",EDGE,"E157")])],"isStart":true});
            chamfer(context, id + "F22", {"entities" : qUnion([Q0, Q1, Q2, Q3]), "chamferType" : ChamferType.TWO_OFFSETS, "width1" : 5.08 * mm, "oppositeDirection" : false, "width2" : 7.62 * mm, "tangentPropagation" : true});
        }
        {
            var Q0;
            Q0=makeQuery(id+"F19.imprint","IMPRINT",FACE,{"disambiguationData":[TD([[makeQuery(id+"F19.imprint","IMPRINT",EDGE,{"derivedFrom":sQuery(id+"F19.wireOp",EDGE,"E182")}),1.0]])]});
            extrude(context, id + "F23", {"entities" : qUnion([Q0]), "depth" : 17.78 * mm, "offsetDistance" : 25.4 * mm});
        }
        {
            var Q0;
            Q0=makeQuery(id+"F20.opExtrude","CAP_EDGE",EDGE,{"disambiguationData":[OSD([sQuery(id+"F19.wireOp",EDGE,"E150")])],"isStart":false});
            chamfer(context, id + "F24", {"entities" : qUnion([Q0]), "chamferType" : ChamferType.TWO_OFFSETS, "width1" : 12.7 * mm, "oppositeDirection" : false, "width2" : 5.08 * mm, "tangentPropagation" : true});
        }
        {
            var Q0;
            Q0=qCreatedBy(makeId("Top.planeOp"),FACE);
            var sketch = newSketch(context, id + "F25", { "sketchPlane" : qUnion([Q0])});
            skArc(sketch, "E183", {"start": v(-327.26, 27.01) * mm, "mid": v(-282.25, 12.88) * mm, "end": v(-235.43, 7.07) * mm});
            skArc(sketch, "E184", {"start": v(-235.43, 7.07) * mm, "mid": v(-172.5, 5.47) * mm, "end": v(-109.56, 7.07) * mm});
            skArc(sketch, "E185", {"start": v(-248.92, 49.22) * mm, "mid": v(-289.25, 42.23) * mm, "end": v(-327.26, 27.01) * mm});
            skArc(sketch, "E186", {"start": v(-248.92, 49.22) * mm, "mid": v(-185.92, 52.95) * mm, "end": v(-123.4, 61.52) * mm});
            skLineSegment(sketch, "E187", {"start": v(-123.4, 61.52) * mm, "end": v(-24.01, 69.4) * mm});
            skLineSegment(sketch, "E188", {"start": v(-24.01, 69.4) * mm, "end": v(34.25, 69.4) * mm});
            skLineSegment(sketch, "E189", {"start": v(-107.81, 25.74) * mm, "end": v(-109.56, 7.07) * mm});
            skArc(sketch, "E190", {"start": v(-93.5, 40.4) * mm, "mid": v(-103.25, 35.6) * mm, "end": v(-107.81, 25.74) * mm});
            skCircle(sketch, "E191", {"center": v(-38.57, 55.85) * mm, "radius": 4.76 * mm});
            skCircle(sketch, "E192", {"center": v(14.6, 54.9) * mm, "radius": 4.76 * mm});
            skCircle(sketch, "E193", {"center": v(-91.45, 52.47) * mm, "radius": 4.76 * mm});
            skArc(sketch, "E194", {"start": v(-43.86, 42.92) * mm, "mid": v(-68.72, 42.49) * mm, "end": v(-93.5, 40.4) * mm});
            skArc(sketch, "E195", {"start": v(-0.83, 47.96) * mm, "mid": v(-12.27, 49.34) * mm, "end": v(-23.8, 49.28) * mm});
            skArc(sketch, "E196", {"start": v(0, 63.67) * mm, "mid": v(-12.52, 64.47) * mm, "end": v(-25.06, 64.65) * mm});
            skLineSegment(sketch, "E197", {"start": v(-76.37, 47.71) * mm, "end": v(-52.88, 48.44) * mm});
            skLineSegment(sketch, "E198", {"start": v(-78, 60.93) * mm, "end": v(-53.7, 62.62) * mm});
            skArc(sketch, "E199", {"start": v(-49.68, 58.3) * mm, "mid": v(-50.66, 61.42) * mm, "end": v(-53.7, 62.62) * mm});
            skArc(sketch, "E200", {"start": v(-52.88, 48.44) * mm, "mid": v(-50.23, 49.74) * mm, "end": v(-49.47, 52.59) * mm});
            skArc(sketch, "E201", {"start": v(-78, 60.93) * mm, "mid": v(-80.58, 59.32) * mm, "end": v(-80.67, 56.28) * mm});
            skArc(sketch, "E202", {"start": v(-80.08, 51.35) * mm, "mid": v(-79, 48.74) * mm, "end": v(-76.37, 47.71) * mm});
            skArc(sketch, "E203", {"start": v(-49.68, 58.3) * mm, "mid": v(-49.94, 55.43) * mm, "end": v(-49.47, 52.59) * mm});
            skArc(sketch, "E204", {"start": v(-80.08, 51.35) * mm, "mid": v(-80.13, 53.84) * mm, "end": v(-80.67, 56.28) * mm});
            skArc(sketch, "E205", {"start": v(-25.06, 64.65) * mm, "mid": v(-27.63, 63.28) * mm, "end": v(-28.14, 60.41) * mm});
            skArc(sketch, "E206", {"start": v(-27.43, 53.5) * mm, "mid": v(-26.64, 50.5) * mm, "end": v(-23.8, 49.28) * mm});
            skArc(sketch, "E207", {"start": v(-27.43, 53.5) * mm, "mid": v(-27.23, 57.01) * mm, "end": v(-28.14, 60.41) * mm});
            skArc(sketch, "E208", {"start": v(3.59, 58.3) * mm, "mid": v(2.95, 61.76) * mm, "end": v(0, 63.67) * mm});
            skArc(sketch, "E209", {"start": v(-0.83, 47.96) * mm, "mid": v(2.5, 49.14) * mm, "end": v(3.3, 52.59) * mm});
            skArc(sketch, "E210", {"start": v(3.59, 58.3) * mm, "mid": v(3.07, 55.47) * mm, "end": v(3.3, 52.59) * mm});
            skArc(sketch, "E211", {"start": v(20.37, 36.9) * mm, "mid": v(-11.46, 42.97) * mm, "end": v(-43.86, 42.92) * mm});
            skArc(sketch, "E212", {"start": v(20.37, 36.9) * mm, "mid": v(32.03, 51.14) * mm, "end": v(34.25, 69.4) * mm});
            skArc(sketch, "E213", {"start": v(-111.45, 62.47) * mm, "mid": v(-106.46, 49.93) * mm, "end": v(-98.73, 38.87) * mm});
            skArc(sketch, "E214", {"start": v(-98.73, 38.87) * mm, "mid": v(-104.61, 32.66) * mm, "end": v(-106.6, 24.34) * mm});
            skLineSegment(sketch, "E215", {"start": v(-106.6, 24.34) * mm, "end": v(-106.13, 7.13) * mm});
            skLineSegment(sketch, "E216", {"start": v(-106.13, 7.13) * mm, "end": v(-109.56, 7.07) * mm});
            skSolve(sketch);
        }
        {
            var Q0;
            Q0=makeQuery(id+"F25.imprint","IMPRINT",FACE,{"disambiguationData":[TD([[makeQuery(id+"F25.imprint","IMPRINT",EDGE,{"derivedFrom":sQuery(id+"F25.wireOp",EDGE,"E183")}),1.0]])]});
            var Q1;
            {var subQ3=sQuery(id+"F25.wireOp",EDGE,"E188");Q1=makeQuery(id+"F25.imprint","IMPRINT",FACE,{"disambiguationData":[TD([[makeQuery(id+"F25.imprint","IMPRINT",EDGE,{"derivedFrom":subQ3}),-1.0]])]});}
            var Q2;
            {var subQ2=sQuery(id+"F25.wireOp",EDGE,"E189");Q2=makeQuery(id+"F25.imprint","IMPRINT",FACE,{"disambiguationData":[TD([[makeQuery(id+"F25.imprint","IMPRINT",EDGE,{"derivedFrom":subQ2}),1.0]])]});}
            extrude(context, id + "F26", {"entities" : qUnion([Q0, Q1, Q2]), "depth" : 2.54 * mm, "offsetDistance" : 25.4 * mm});
        }
        {
            var Q0;
            Q0=qCreatedBy(makeId("Top.planeOp"),FACE);
            var sketch = newSketch(context, id + "F27", { "sketchPlane" : qUnion([Q0])});
            skLineSegment(sketch, "E217", {"start": v(-162.23, -37.01) * mm, "end": v(-103.96, -37.01) * mm});
            skLineSegment(sketch, "E218", {"start": v(-246.03, -80.68) * mm, "end": v(-247.78, -99.34) * mm});
            skArc(sketch, "E219", {"start": v(-231.72, -66.02) * mm, "mid": v(-241.47, -70.82) * mm, "end": v(-246.03, -80.68) * mm});
            skCircle(sketch, "E220", {"center": v(-176.78, -50.57) * mm, "radius": 4.76 * mm});
            skCircle(sketch, "E221", {"center": v(-123.61, -51.53) * mm, "radius": 4.76 * mm});
            skCircle(sketch, "E222", {"center": v(-229.66, -53.95) * mm, "radius": 4.76 * mm});
            skArc(sketch, "E223", {"start": v(-182.07, -63.5) * mm, "mid": v(-206.94, -63.93) * mm, "end": v(-231.72, -66.02) * mm});
            skArc(sketch, "E224", {"start": v(-139.04, -58.46) * mm, "mid": v(-150.48, -57.08) * mm, "end": v(-162.01, -57.14) * mm});
            skArc(sketch, "E225", {"start": v(-138.21, -42.75) * mm, "mid": v(-150.73, -41.95) * mm, "end": v(-163.27, -41.77) * mm});
            skLineSegment(sketch, "E226", {"start": v(-214.58, -58.7) * mm, "end": v(-191.1, -57.98) * mm});
            skLineSegment(sketch, "E227", {"start": v(-216.21, -45.5) * mm, "end": v(-191.91, -43.8) * mm});
            skArc(sketch, "E228", {"start": v(-187.9, -48.11) * mm, "mid": v(-188.87, -45) * mm, "end": v(-191.91, -43.8) * mm});
            skArc(sketch, "E229", {"start": v(-191.1, -57.98) * mm, "mid": v(-188.45, -56.68) * mm, "end": v(-187.68, -53.83) * mm});
            skArc(sketch, "E230", {"start": v(-216.21, -45.5) * mm, "mid": v(-218.79, -47.1) * mm, "end": v(-218.88, -50.14) * mm});
            skArc(sketch, "E231", {"start": v(-218.29, -55.07) * mm, "mid": v(-217.2, -57.68) * mm, "end": v(-214.58, -58.7) * mm});
            skArc(sketch, "E232", {"start": v(-187.9, -48.11) * mm, "mid": v(-188.15, -50.98) * mm, "end": v(-187.68, -53.83) * mm});
            skArc(sketch, "E233", {"start": v(-218.29, -55.07) * mm, "mid": v(-218.35, -52.58) * mm, "end": v(-218.88, -50.14) * mm});
            skArc(sketch, "E234", {"start": v(-163.27, -41.77) * mm, "mid": v(-165.85, -43.14) * mm, "end": v(-166.36, -46) * mm});
            skArc(sketch, "E235", {"start": v(-165.65, -52.93) * mm, "mid": v(-164.85, -55.91) * mm, "end": v(-162.01, -57.14) * mm});
            skArc(sketch, "E236", {"start": v(-165.65, -52.93) * mm, "mid": v(-165.44, -49.4) * mm, "end": v(-166.36, -46) * mm});
            skArc(sketch, "E237", {"start": v(-134.63, -48.11) * mm, "mid": v(-135.26, -44.66) * mm, "end": v(-138.21, -42.75) * mm});
            skArc(sketch, "E238", {"start": v(-139.04, -58.46) * mm, "mid": v(-135.7, -57.28) * mm, "end": v(-134.91, -53.83) * mm});
            skArc(sketch, "E239", {"start": v(-134.63, -48.11) * mm, "mid": v(-135.15, -50.95) * mm, "end": v(-134.91, -53.83) * mm});
            skArc(sketch, "E240", {"start": v(-117.84, -69.53) * mm, "mid": v(-149.67, -63.45) * mm, "end": v(-182.07, -63.5) * mm});
            skArc(sketch, "E241", {"start": v(-117.84, -69.53) * mm, "mid": v(-106.18, -55.28) * mm, "end": v(-103.96, -37.01) * mm});
            skArc(sketch, "E242", {"start": v(-249.66, -43.95) * mm, "mid": v(-244.67, -56.49) * mm, "end": v(-236.94, -67.55) * mm});
            skArc(sketch, "E243", {"start": v(-471.85, -145.4) * mm, "mid": v(-426.85, -159.53) * mm, "end": v(-380.03, -165.34) * mm});
            skArc(sketch, "E244", {"start": v(-380.03, -165.34) * mm, "mid": v(-317.1, -166.94) * mm, "end": v(-254.16, -165.34) * mm});
            skArc(sketch, "E245", {"start": v(-393.51, -123.19) * mm, "mid": v(-433.85, -130.18) * mm, "end": v(-471.85, -145.4) * mm});
            skArc(sketch, "E246", {"start": v(-393.51, -123.19) * mm, "mid": v(-330.52, -119.46) * mm, "end": v(-268, -110.89) * mm});
            skLineSegment(sketch, "E247", {"start": v(-268, -110.89) * mm, "end": v(-168.61, -103) * mm});
            skLineSegment(sketch, "E248", {"start": v(-168.61, -103) * mm, "end": v(-110.35, -103) * mm});
            skLineSegment(sketch, "E249", {"start": v(-252.41, -146.67) * mm, "end": v(-254.16, -165.34) * mm});
            skArc(sketch, "E250", {"start": v(-238.1, -132.02) * mm, "mid": v(-247.85, -136.81) * mm, "end": v(-252.41, -146.67) * mm});
            skCircle(sketch, "E251", {"center": v(-183.17, -116.57) * mm, "radius": 4.76 * mm});
            skCircle(sketch, "E252", {"center": v(-130, -117.52) * mm, "radius": 4.76 * mm});
            skCircle(sketch, "E253", {"center": v(-236.05, -119.94) * mm, "radius": 4.76 * mm});
            skArc(sketch, "E254", {"start": v(-188.45, -129.5) * mm, "mid": v(-213.32, -129.92) * mm, "end": v(-238.1, -132.02) * mm});
            skArc(sketch, "E255", {"start": v(-145.43, -124.46) * mm, "mid": v(-156.87, -123.07) * mm, "end": v(-168.4, -123.13) * mm});
            skArc(sketch, "E256", {"start": v(-144.6, -108.74) * mm, "mid": v(-157.12, -107.94) * mm, "end": v(-169.66, -107.77) * mm});
            skLineSegment(sketch, "E257", {"start": v(-220.97, -124.7) * mm, "end": v(-197.48, -123.98) * mm});
            skLineSegment(sketch, "E258", {"start": v(-222.6, -111.48) * mm, "end": v(-198.3, -109.8) * mm});
            skArc(sketch, "E259", {"start": v(-194.28, -114.1) * mm, "mid": v(-195.26, -110.99) * mm, "end": v(-198.3, -109.8) * mm});
            skArc(sketch, "E260", {"start": v(-197.48, -123.98) * mm, "mid": v(-194.83, -122.67) * mm, "end": v(-194.07, -119.82) * mm});
            skArc(sketch, "E261", {"start": v(-222.6, -111.48) * mm, "mid": v(-225.17, -113.1) * mm, "end": v(-225.27, -116.14) * mm});
            skArc(sketch, "E262", {"start": v(-224.67, -121.07) * mm, "mid": v(-223.6, -123.67) * mm, "end": v(-220.97, -124.7) * mm});
            skArc(sketch, "E263", {"start": v(-194.28, -114.1) * mm, "mid": v(-194.54, -116.98) * mm, "end": v(-194.07, -119.82) * mm});
            skArc(sketch, "E264", {"start": v(-224.67, -121.07) * mm, "mid": v(-224.73, -118.57) * mm, "end": v(-225.27, -116.14) * mm});
            skArc(sketch, "E265", {"start": v(-169.66, -107.77) * mm, "mid": v(-172.23, -109.13) * mm, "end": v(-172.74, -112) * mm});
            skArc(sketch, "E266", {"start": v(-172.03, -118.92) * mm, "mid": v(-171.24, -121.9) * mm, "end": v(-168.4, -123.13) * mm});
            skArc(sketch, "E267", {"start": v(-172.03, -118.92) * mm, "mid": v(-171.83, -115.4) * mm, "end": v(-172.74, -112) * mm});
            skArc(sketch, "E268", {"start": v(-141.01, -114.1) * mm, "mid": v(-141.65, -110.65) * mm, "end": v(-144.6, -108.74) * mm});
            skArc(sketch, "E269", {"start": v(-145.43, -124.46) * mm, "mid": v(-142.09, -123.27) * mm, "end": v(-141.3, -119.82) * mm});
            skArc(sketch, "E270", {"start": v(-141.01, -114.1) * mm, "mid": v(-141.53, -116.95) * mm, "end": v(-141.3, -119.82) * mm});
            skArc(sketch, "E271", {"start": v(-124.23, -135.52) * mm, "mid": v(-156.06, -129.44) * mm, "end": v(-188.45, -129.5) * mm});
            skArc(sketch, "E272", {"start": v(-124.23, -135.52) * mm, "mid": v(-112.57, -121.28) * mm, "end": v(-110.35, -103) * mm});
            skArc(sketch, "E273", {"start": v(-256.05, -109.94) * mm, "mid": v(-251.05, -122.48) * mm, "end": v(-243.32, -133.55) * mm});
            skCircle(sketch, "E274", {"center": v(-123.36, -81.85) * mm, "radius": 4.76 * mm});
            skLineSegment(sketch, "E275", {"start": v(-247.78, -99.34) * mm, "end": v(-299.94, -98.39) * mm});
            skLineSegment(sketch, "E276", {"start": v(-103.96, -37.01) * mm, "end": v(-166.73, -37.01) * mm});
            skLineSegment(sketch, "E277", {"start": v(-166.73, -37.01) * mm, "end": v(-421.36, -57.57) * mm});
            skArc(sketch, "E278", {"start": v(-511.74, -70.61) * mm, "mid": v(-406.74, -91.36) * mm, "end": v(-299.94, -98.39) * mm});
            skArc(sketch, "E279", {"start": v(-421.36, -57.57) * mm, "mid": v(-466.75, -62.67) * mm, "end": v(-511.74, -70.61) * mm});
            skSolve(sketch);
        }
        {
            var Q0;
            Q0=makeQuery(id+"F26.opExtrude","CAP_EDGE",EDGE,{"disambiguationData":[OSD([sQuery(id+"F25.wireOp",EDGE,"E183")])],"isStart":false});
            var Q1;
            Q1=makeQuery(id+"F26.opExtrude","CAP_EDGE",EDGE,{"disambiguationData":[OSD([sQuery(id+"F25.wireOp",EDGE,"E183")])],"isStart":true});
            chamfer(context, id + "F28", {"entities" : qUnion([Q0, Q1]), "chamferType" : ChamferType.TWO_OFFSETS, "width1" : 30.48 * mm, "oppositeDirection" : false, "width2" : 1.14 * mm, "tangentPropagation" : true});
        }
        {
            var Q0;
            Q0=makeQuery(id+"F27.imprint","IMPRINT",FACE,{"disambiguationData":[TD([[makeQuery(id+"F27.imprint","IMPRINT",EDGE,{"derivedFrom":sQuery(id+"F27.wireOp",EDGE,"E274")}),1.0]])]});
            extrude(context, id + "F29", {"entities" : qUnion([Q0]), "depth" : 5.08 * mm, "offsetDistance" : 25.4 * mm});
        }
        {
            var Q0;
            Q0=qCreatedBy(makeId("Top.planeOp"),FACE);
            var sketch = newSketch(context, id + "F30", { "sketchPlane" : qUnion([Q0])});
            skArc(sketch, "E280", {"start": v(-51.42, -261.32) * mm, "mid": v(11.52, -262.92) * mm, "end": v(74.45, -261.32) * mm});
            skLineSegment(sketch, "E281", {"start": v(160, -198.98) * mm, "end": v(218.26, -198.98) * mm});
            skArc(sketch, "E282", {"start": v(204.93, -232.42) * mm, "mid": v(172.74, -227.28) * mm, "end": v(140.16, -228) * mm});
            skArc(sketch, "E283", {"start": v(204.93, -232.42) * mm, "mid": v(216.44, -217.63) * mm, "end": v(218.26, -198.98) * mm});
            skLineSegment(sketch, "E284", {"start": v(74.45, -261.32) * mm, "end": v(75.94, -245.18) * mm});
            skCircle(sketch, "E285", {"center": v(198.88, -214.72) * mm, "radius": 4.7 * mm});
            skCircle(sketch, "E286", {"center": v(145.6, -213.8) * mm, "radius": 4.7 * mm});
            skArc(sketch, "E287", {"start": v(184.8, -222.53) * mm, "mid": v(172.1, -221.07) * mm, "end": v(159.34, -220.79) * mm});
            skArc(sketch, "E288", {"start": v(185.57, -205.6) * mm, "mid": v(171.8, -204.6) * mm, "end": v(158, -204.48) * mm});
            skLineSegment(sketch, "E289", {"start": v(105.29, -208.15) * mm, "end": v(130.47, -206.37) * mm});
            skArc(sketch, "E290", {"start": v(105.29, -208.15) * mm, "mid": v(102.8, -209.6) * mm, "end": v(102.44, -212.46) * mm});
            skArc(sketch, "E291", {"start": v(135.11, -211.25) * mm, "mid": v(133.94, -207.72) * mm, "end": v(130.47, -206.37) * mm});
            skArc(sketch, "E292", {"start": v(131.28, -221.26) * mm, "mid": v(134.34, -219.71) * mm, "end": v(135.12, -216.37) * mm});
            skArc(sketch, "E293", {"start": v(135.11, -211.25) * mm, "mid": v(134.8, -213.81) * mm, "end": v(135.12, -216.37) * mm});
            skArc(sketch, "E294", {"start": v(158, -204.48) * mm, "mid": v(155.43, -205.93) * mm, "end": v(155.2, -208.87) * mm});
            skArc(sketch, "E295", {"start": v(155.99, -216.7) * mm, "mid": v(156.65, -219.58) * mm, "end": v(159.34, -220.79) * mm});
            skArc(sketch, "E296", {"start": v(155.99, -216.7) * mm, "mid": v(156.34, -212.71) * mm, "end": v(155.2, -208.87) * mm});
            skArc(sketch, "E297", {"start": v(188.9, -210.6) * mm, "mid": v(188.42, -207.31) * mm, "end": v(185.57, -205.6) * mm});
            skArc(sketch, "E298", {"start": v(184.8, -222.53) * mm, "mid": v(187.86, -221.4) * mm, "end": v(188.68, -218.24) * mm});
            skArc(sketch, "E299", {"start": v(188.9, -210.6) * mm, "mid": v(188.08, -214.4) * mm, "end": v(188.68, -218.24) * mm});
            skLineSegment(sketch, "E300", {"start": v(74.45, -261.32) * mm, "end": v(76.37, -240.44) * mm});
            skLineSegment(sketch, "E301", {"start": v(90.34, -227.99) * mm, "end": v(140.16, -228) * mm});
            skArc(sketch, "E302", {"start": v(90.34, -227.99) * mm, "mid": v(80.9, -231.46) * mm, "end": v(76.37, -240.44) * mm});
            skArc(sketch, "E303", {"start": v(-156.34, -235.23) * mm, "mid": v(-105.07, -253.04) * mm, "end": v(-51.42, -261.32) * mm});
            skArc(sketch, "E304", {"start": v(-79.4, -217.97) * mm, "mid": v(-118.57, -223.48) * mm, "end": v(-156.34, -235.23) * mm});
            skLineSegment(sketch, "E305", {"start": v(-79.4, -217.97) * mm, "end": v(160, -198.98) * mm});
            skCircle(sketch, "E306", {"center": v(92.8, -216.15) * mm, "radius": 4.76 * mm});
            skLineSegment(sketch, "E307", {"start": v(131.28, -221.26) * mm, "end": v(106.27, -221.26) * mm});
            skArc(sketch, "E308", {"start": v(103.12, -217.4) * mm, "mid": v(103.78, -220.08) * mm, "end": v(106.27, -221.26) * mm});
            skArc(sketch, "E309", {"start": v(103.12, -217.4) * mm, "mid": v(103.08, -214.9) * mm, "end": v(102.44, -212.46) * mm});
            skSolve(sketch);
        }
        {
            var Q0;
            {var subQ0=sQuery(id+"F30.wireOp",EDGE,"E280");Q0=makeQuery(id+"F30.imprint","IMPRINT",FACE,{"disambiguationData":[TD([[makeQuery(id+"F30.imprint","IMPRINT",EDGE,{"derivedFrom":subQ0}),1.0]])]});}
            extrude(context, id + "F31", {"entities" : qUnion([Q0]), "depth" : 2.8 * mm, "offsetDistance" : 25.4 * mm});
        }
        {
            var Q0;
            Q0=makeQuery(id+"F31.opExtrude","CAP_EDGE",EDGE,{"disambiguationData":[OSD([sQuery(id+"F30.wireOp",EDGE,"E280")])],"isStart":false});
            var Q1;
            Q1=makeQuery(id+"F31.opExtrude","CAP_EDGE",EDGE,{"disambiguationData":[OSD([sQuery(id+"F30.wireOp",EDGE,"E280")])],"isStart":true});
            var Q2;
            Q2=makeQuery(id+"F31.opExtrude","CAP_EDGE",EDGE,{"disambiguationData":[OSD([sQuery(id+"F30.wireOp",EDGE,"E303")])],"isStart":false});
            var Q3;
            Q3=makeQuery(id+"F31.opExtrude","CAP_EDGE",EDGE,{"disambiguationData":[OSD([sQuery(id+"F30.wireOp",EDGE,"E303")])],"isStart":true});
            chamfer(context, id + "F32", {"entities" : qUnion([Q0, Q1, Q2, Q3]), "chamferType" : ChamferType.TWO_OFFSETS, "width1" : 30.48 * mm, "oppositeDirection" : false, "width2" : 1.27 * mm, "tangentPropagation" : true});
        }
        {
            var Q0;
            {var subQ4=sQuery(id+"F27.wireOp",EDGE,"E218");Q0=makeQuery(id+"F27.imprint","IMPRINT",FACE,{"disambiguationData":[TD([[makeQuery(id+"F27.imprint","IMPRINT",EDGE,{"derivedFrom":subQ4}),-1.0]])]});}
            extrude(context, id + "F33", {"entities" : qUnion([Q0]), "depth" : 2.54 * mm, "offsetDistance" : 25.4 * mm});
        }
        {
            var Q0;
            Q0=makeQuery(id+"F33.opExtrude","CAP_EDGE",EDGE,{"disambiguationData":[OSD([sQuery(id+"F27.wireOp",EDGE,"rFbFL4Rl-Fqbm-kJ4N-jmw8-Qa1jP6Q9Brae")])],"isStart":false});
            var Q1;
            Q1=makeQuery(id+"F33.opExtrude","CAP_EDGE",EDGE,{"disambiguationData":[OSD([sQuery(id+"F27.wireOp",EDGE,"rFbFL4Rl-Fqbm-kJ4N-jmw8-Qa1jP6Q9Brae")])],"isStart":true});
            var Q2;
            Q2=makeQuery(id+"F33.opExtrude","CAP_EDGE",EDGE,{"disambiguationData":[OSD([sQuery(id+"F27.wireOp",EDGE,"E278")])],"isStart":false});
            var Q3;
            Q3=makeQuery(id+"F33.opExtrude","CAP_EDGE",EDGE,{"disambiguationData":[OSD([sQuery(id+"F27.wireOp",EDGE,"E278")])],"isStart":true});
            chamfer(context, id + "F34", {"entities" : qUnion([Q0, Q1, Q2, Q3]), "chamferType" : ChamferType.TWO_OFFSETS, "width1" : 30.48 * mm, "oppositeDirection" : false, "width2" : 1.27 * mm, "tangentPropagation" : true});
        }
        {
            var Q0;
            {var subQ3=sQuery(id+"F27.wireOp",EDGE,"E248");Q0=makeQuery(id+"F27.imprint","IMPRINT",FACE,{"disambiguationData":[TD([[makeQuery(id+"F27.imprint","IMPRINT",EDGE,{"derivedFrom":subQ3}),-1.0]])]});}
            var Q1;
            Q1=makeQuery(id+"F27.imprint","IMPRINT",FACE,{"disambiguationData":[TD([[makeQuery(id+"F27.imprint","IMPRINT",EDGE,{"derivedFrom":sQuery(id+"F27.wireOp",EDGE,"E257")}),1.0]])]});
            var Q2;
            Q2=makeQuery(id+"F27.imprint","IMPRINT",FACE,{"disambiguationData":[TD([[makeQuery(id+"F27.imprint","IMPRINT",EDGE,{"derivedFrom":sQuery(id+"F27.wireOp",EDGE,"E255")}),-1.0]])]});
            extrude(context, id + "F35", {"entities" : qUnion([Q0, Q1, Q2]), "depth" : 7.62 * mm, "offsetDistance" : 25.4 * mm});
        }
        {
            var Q0;
            Q0=makeQuery(id+"F35.opExtrude","CAP_EDGE",EDGE,{"disambiguationData":[OSD([sQuery(id+"F27.wireOp",EDGE,"E254")])],"isStart":false});
            var Q1;
            Q1=makeQuery(id+"F35.opExtrude","CAP_EDGE",EDGE,{"disambiguationData":[OSD([sQuery(id+"F27.wireOp",EDGE,"E271")])],"isStart":false});
            var Q2;
            Q2=makeQuery(id+"F35.opExtrude","CAP_EDGE",EDGE,{"disambiguationData":[OSD([sQuery(id+"F27.wireOp",EDGE,"E273")])],"isStart":false});
            chamfer(context, id + "F36", {"entities" : qUnion([Q0, Q1, Q2]), "chamferType" : ChamferType.TWO_OFFSETS, "width1" : 6.35 * mm, "oppositeDirection" : false, "width2" : 10.16 * mm, "tangentPropagation" : true});
        }
        {
            var Q0;
            Q0=makeQuery(id+"F35.opExtrude","CAP_EDGE",EDGE,{"disambiguationData":[OSD([sQuery(id+"F27.wireOp",EDGE,"E247")])],"isStart":false});
            var Q1;
            Q1=makeQuery(id+"F35.opExtrude","CAP_EDGE",EDGE,{"disambiguationData":[OSD([sQuery(id+"F27.wireOp",EDGE,"E248")])],"isStart":false});
            chamfer(context, id + "F37", {"entities" : qUnion([Q0, Q1]), "width" : 5.08 * mm, "tangentPropagation" : true});
        }
        {
            var Q0;
            Q0=qCreatedBy(makeId("Top.planeOp"),FACE);
            var sketch = newSketch(context, id + "F38", { "sketchPlane" : qUnion([Q0])});
            skLineSegment(sketch, "E310", {"start": v(417.03, -38.8) * mm, "end": v(417.03, -48.96) * mm});
            skArc(sketch, "E311", {"start": v(427.2, -38.71) * mm, "mid": v(420, -41.74) * mm, "end": v(417.03, -48.96) * mm});
            skLineSegment(sketch, "E312", {"start": v(283.49, -29.27) * mm, "end": v(473.81, -13.76) * mm});
            skArc(sketch, "E313", {"start": v(493.93, -13.31) * mm, "mid": v(483.87, -13.24) * mm, "end": v(473.81, -13.76) * mm});
            skArc(sketch, "E314", {"start": v(493.93, -13.31) * mm, "mid": v(513, -13.37) * mm, "end": v(532.06, -12.76) * mm});
            skLineSegment(sketch, "E315", {"start": v(417.03, -48.96) * mm, "end": v(417.03, -58.08) * mm});
            skArc(sketch, "E316", {"start": v(415.8, -73.73) * mm, "mid": v(416.72, -65.93) * mm, "end": v(417.03, -58.08) * mm});
            skArc(sketch, "E317", {"start": v(522.6, -41.46) * mm, "mid": v(494.44, -37.34) * mm, "end": v(466, -38.34) * mm});
            skLineSegment(sketch, "E318", {"start": v(466, -38.34) * mm, "end": v(427.2, -38.71) * mm});
            skArc(sketch, "E319", {"start": v(522.6, -41.46) * mm, "mid": v(531.94, -28.63) * mm, "end": v(532.06, -12.76) * mm});
            skLineSegment(sketch, "E320", {"start": v(420, -41.74) * mm, "end": v(408.16, -26.65) * mm});
            skLineSegment(sketch, "E321", {"start": v(408.16, -26.65) * mm, "end": v(405.47, -19.33) * mm});
            skArc(sketch, "E322", {"start": v(283.49, -29.27) * mm, "mid": v(229.16, -36.27) * mm, "end": v(175.73, -48.33) * mm});
            skArc(sketch, "E323", {"start": v(175.73, -48.33) * mm, "mid": v(294.97, -68.57) * mm, "end": v(415.8, -73.73) * mm});
            skSolve(sketch);
        }
        {
            var Q0;
            {var subQ0=sQuery(id+"F38.wireOp",EDGE,"xrM6mkdu-LN4g-Sa3Q-6pfD-6GRJu8MGDRnw");Q0=makeQuery(id+"F38.imprint","IMPRINT",FACE,{"disambiguationData":[TD([[makeQuery(id+"F38.imprint","IMPRINT",EDGE,{"derivedFrom":subQ0}),1.0]])]});}
            var Q1;
            {var subQ1=sQuery(id+"F38.wireOp",EDGE,"fYEpZVfg-rEje-WGa1-Ds73-3jGjzIPJSpYN");var subQ3=makeQuery(id+"F38.imprint","INTERSECT",VERTEX,{"derivedFrom":[subQ1,sQuery(id+"F38.wireOp",EDGE,"PCUdtxBE-lNNZ-n4kL-9igX-TXOqFITGSbMh")]});Q1=makeQuery(id+"F38.imprint","IMPRINT",FACE,{"disambiguationData":[TD([[makeQuery(id+"F38.imprint","IMPRINT",EDGE,{"disambiguationData":[TD([[subQ3,1.0]])],"derivedFrom":subQ1}),1.0]])]});}
            var Q2;
            {var subQ0=sQuery(id+"F38.wireOp",EDGE,"N5DQppKd-rI9l-P7B3-b6aM-Iujkp348vSaM");Q2=makeQuery(id+"F38.imprint","IMPRINT",FACE,{"disambiguationData":[TD([[makeQuery(id+"F38.imprint","IMPRINT",EDGE,{"derivedFrom":subQ0}),1.0]])]});}
            var Q3;
            {var subQ0=sQuery(id+"F38.wireOp",EDGE,"PCUdtxBE-lNNZ-n4kL-9igX-TXOqFITGSbMh");var subQ1=sQuery(id+"F38.wireOp",EDGE,"fYEpZVfg-rEje-WGa1-Ds73-3jGjzIPJSpYN");var subQ2=makeQuery(id+"F38.imprint","INTERSECT",VERTEX,{"derivedFrom":[subQ1,subQ0]});Q3=makeQuery(id+"F38.imprint","IMPRINT",FACE,{"disambiguationData":[TD([[makeQuery(id+"F38.imprint","IMPRINT",EDGE,{"disambiguationData":[TD([[subQ2,1.0]])],"derivedFrom":subQ1}),-1.0]])]});}
            var Q4;
            {var subQ8=sQuery(id+"F38.wireOp",EDGE,"N5DQppKd-rI9l-P7B3-b6aM-Iujkp348vSaM");Q4=makeQuery(id+"F38.imprint","IMPRINT",FACE,{"disambiguationData":[TD([[makeQuery(id+"F38.imprint","IMPRINT",EDGE,{"derivedFrom":subQ8}),-1.0]])]});}
            var Q5;
            {var subQ0=sQuery(id+"F38.wireOp",EDGE,"NXFCrZig-Mi3s-3Pw2-SaoM-fHpFLn5GzYdL");var subQ1=sQuery(id+"F38.wireOp",EDGE,"HEw00yZZ-UeAW-jDKk-sJWR-eoWo8ZVfU7I0");var subQ2=makeQuery(id+"F38.imprint","INTERSECT",VERTEX,{"derivedFrom":[subQ1,subQ0]});Q5=makeQuery(id+"F38.imprint","IMPRINT",FACE,{"disambiguationData":[TD([[makeQuery(id+"F38.imprint","IMPRINT",EDGE,{"disambiguationData":[TD([[subQ2,-1.0]])],"derivedFrom":subQ1}),-1.0]])]});}
            var Q6;
            {var subQ0=sQuery(id+"F38.wireOp",EDGE,"E310");Q6=makeQuery(id+"F38.imprint","IMPRINT",FACE,{"disambiguationData":[TD([[makeQuery(id+"F38.imprint","IMPRINT",EDGE,{"derivedFrom":subQ0}),1.0]])]});}
            var Q7;
            {var subQ3=sQuery(id+"F38.wireOp",EDGE,"E310");Q7=makeQuery(id+"F38.imprint","IMPRINT",FACE,{"disambiguationData":[TD([[makeQuery(id+"F38.imprint","IMPRINT",EDGE,{"derivedFrom":subQ3}),-1.0]])]});}
            var Q8;
            {var subQ4=sQuery(id+"F38.wireOp",EDGE,"E315");Q8=makeQuery(id+"F38.imprint","IMPRINT",FACE,{"disambiguationData":[TD([[makeQuery(id+"F38.imprint","IMPRINT",EDGE,{"derivedFrom":subQ4}),-1.0]])]});}
            var Q9;
            {var subQ0=sQuery(id+"F38.wireOp",EDGE,"E313");Q9=makeQuery(id+"F38.imprint","IMPRINT",FACE,{"disambiguationData":[TD([[makeQuery(id+"F38.imprint","IMPRINT",EDGE,{"derivedFrom":subQ0}),1.0]])]});}
            extrude(context, id + "F39", {"entities" : qUnion([Q0, Q1, Q2, Q3, Q4, Q5, Q6, Q7, Q8, Q9]), "depth" : 2.54 * mm, "offsetDistance" : 25.4 * mm});
        }
        {
            var Q0;
            Q0=qCreatedBy(makeId("Top.planeOp"),FACE);
            var sketch = newSketch(context, id + "F40", { "sketchPlane" : qUnion([Q0])});
            skLineSegment(sketch, "E324", {"start": v(374, -155.82) * mm, "end": v(374, -165.97) * mm});
            skArc(sketch, "E325", {"start": v(384.17, -155.72) * mm, "mid": v(376.98, -158.75) * mm, "end": v(374, -165.97) * mm});
            skLineSegment(sketch, "E326", {"start": v(240.46, -146.28) * mm, "end": v(430.79, -130.77) * mm});
            skArc(sketch, "E327", {"start": v(450.91, -130.33) * mm, "mid": v(440.84, -130.25) * mm, "end": v(430.79, -130.77) * mm});
            skArc(sketch, "E328", {"start": v(450.91, -130.33) * mm, "mid": v(469.98, -130.38) * mm, "end": v(489.04, -129.77) * mm});
            skLineSegment(sketch, "E329", {"start": v(374, -165.97) * mm, "end": v(374, -175.09) * mm});
            skArc(sketch, "E330", {"start": v(372.77, -190.74) * mm, "mid": v(373.7, -182.94) * mm, "end": v(374, -175.09) * mm});
            skArc(sketch, "E331", {"start": v(132.71, -171.7) * mm, "mid": v(252.3, -186.76) * mm, "end": v(372.77, -190.74) * mm});
            skArc(sketch, "E332", {"start": v(240.46, -146.28) * mm, "mid": v(185.63, -154.93) * mm, "end": v(132.71, -171.7) * mm});
            skArc(sketch, "E333", {"start": v(479.57, -158.47) * mm, "mid": v(451.42, -154.35) * mm, "end": v(422.99, -155.35) * mm});
            skLineSegment(sketch, "E334", {"start": v(422.99, -155.35) * mm, "end": v(384.17, -155.72) * mm});
            skArc(sketch, "E335", {"start": v(479.57, -158.47) * mm, "mid": v(488.92, -145.64) * mm, "end": v(489.04, -129.77) * mm});
            skLineSegment(sketch, "E336", {"start": v(376.98, -158.75) * mm, "end": v(365.14, -143.66) * mm});
            skLineSegment(sketch, "E337", {"start": v(365.14, -143.66) * mm, "end": v(362.45, -136.34) * mm});
            skLineSegment(sketch, "E338", {"start": v(124.02, -119.63) * mm, "end": v(124.02, -129.79) * mm});
            skArc(sketch, "E339", {"start": v(134.19, -119.54) * mm, "mid": v(127, -122.57) * mm, "end": v(124.02, -129.79) * mm});
            skLineSegment(sketch, "E340", {"start": v(-9.52, -110.1) * mm, "end": v(180.8, -94.59) * mm});
            skArc(sketch, "E341", {"start": v(200.93, -94.14) * mm, "mid": v(190.86, -94.07) * mm, "end": v(180.8, -94.59) * mm});
            skArc(sketch, "E342", {"start": v(200.93, -94.14) * mm, "mid": v(220, -94.2) * mm, "end": v(239.06, -93.59) * mm});
            skLineSegment(sketch, "E343", {"start": v(124.02, -129.79) * mm, "end": v(124.02, -138.9) * mm});
            skArc(sketch, "E344", {"start": v(122.79, -154.55) * mm, "mid": v(123.71, -146.75) * mm, "end": v(124.02, -138.9) * mm});
            skArc(sketch, "E345", {"start": v(-117.27, -135.5) * mm, "mid": v(2.32, -150.57) * mm, "end": v(122.79, -154.55) * mm});
            skArc(sketch, "E346", {"start": v(-9.52, -110.1) * mm, "mid": v(-64.35, -118.75) * mm, "end": v(-117.27, -135.5) * mm});
            skArc(sketch, "E347", {"start": v(229.59, -122.29) * mm, "mid": v(201.44, -118.16) * mm, "end": v(173, -119.17) * mm});
            skLineSegment(sketch, "E348", {"start": v(173, -119.17) * mm, "end": v(134.19, -119.54) * mm});
            skArc(sketch, "E349", {"start": v(229.59, -122.29) * mm, "mid": v(238.93, -109.46) * mm, "end": v(239.06, -93.59) * mm});
            skLineSegment(sketch, "E350", {"start": v(127, -122.57) * mm, "end": v(115.15, -107.48) * mm});
            skLineSegment(sketch, "E351", {"start": v(115.15, -107.48) * mm, "end": v(112.46, -100.16) * mm});
            skSolve(sketch);
        }
        {
            var Q0;
            {var subQ0=sQuery(id+"F40.wireOp",EDGE,"E327");Q0=makeQuery(id+"F40.imprint","IMPRINT",FACE,{"disambiguationData":[TD([[makeQuery(id+"F40.imprint","IMPRINT",EDGE,{"derivedFrom":subQ0}),1.0]])]});}
            var Q1;
            {var subQ0=sQuery(id+"F40.wireOp",EDGE,"E341");Q1=makeQuery(id+"F40.imprint","IMPRINT",FACE,{"disambiguationData":[TD([[makeQuery(id+"F40.imprint","IMPRINT",EDGE,{"derivedFrom":subQ0}),1.0]])]});}
            extrude(context, id + "F41", {"entities" : qUnion([Q0, Q1]), "depth" : 7.62 * mm, "offsetDistance" : 25.4 * mm});
        }
        {
            var Q0;
            Q0=makeQuery(id+"F39.opExtrude","CAP_EDGE",EDGE,{"disambiguationData":[OSD([sQuery(id+"F38.wireOp",EDGE,"lV7nMA89-h3zc-hIQ9-GCaX-6L9lHAtv520D")])],"isStart":false});
            var Q1;
            Q1=makeQuery(id+"F39.opExtrude","CAP_EDGE",EDGE,{"disambiguationData":[OSD([sQuery(id+"F38.wireOp",EDGE,"E323")])],"isStart":false});
            chamfer(context, id + "F42", {"entities" : qUnion([Q0, Q1]), "chamferType" : ChamferType.TWO_OFFSETS, "width1" : 30.48 * mm, "oppositeDirection" : false, "width2" : 1.27 * mm, "tangentPropagation" : true});
        }
        {
            var Q0;
            Q0=makeQuery(id+"F41.opExtrude","CAP_EDGE",EDGE,{"disambiguationData":[OSD([sQuery(id+"F40.wireOp",EDGE,"E333")])],"isStart":false});
            var Q1;
            Q1=makeQuery(id+"F41.opExtrude","CAP_EDGE",EDGE,{"disambiguationData":[OSD([sQuery(id+"F40.wireOp",EDGE,"E334")])],"isStart":false});
            chamfer(context, id + "F43", {"entities" : qUnion([Q0, Q1]), "chamferType" : ChamferType.TWO_OFFSETS, "width1" : 5.08 * mm, "oppositeDirection" : false, "width2" : 10.16 * mm, "tangentPropagation" : true});
        }
        {
            var Q0;
            Q0=makeQuery(id+"F41.opExtrude","CAP_EDGE",EDGE,{"disambiguationData":[OSD([sQuery(id+"F40.wireOp",EDGE,"E326")])],"isStart":false});
            var Q1;
            Q1=makeQuery(id+"F41.opExtrude","CAP_EDGE",EDGE,{"disambiguationData":[OSD([sQuery(id+"F40.wireOp",EDGE,"E328")])],"isStart":false});
            var Q2;
            Q2=makeQuery(id+"F41.opExtrude","CAP_EDGE",EDGE,{"disambiguationData":[OSD([sQuery(id+"F40.wireOp",EDGE,"E327")])],"isStart":false});
            chamfer(context, id + "F44", {"entities" : qUnion([Q0, Q1, Q2]), "chamferType" : ChamferType.TWO_OFFSETS, "width1" : 5.08 * mm, "oppositeDirection" : false, "width2" : 7.62 * mm, "tangentPropagation" : true});
        }
        {
            var Q0;
            Q0=makeQuery(id+"F41.opExtrude","CAP_EDGE",EDGE,{"disambiguationData":[OSD([sQuery(id+"F40.wireOp",EDGE,"E347")])],"isStart":true});
            var Q1;
            Q1=makeQuery(id+"F41.opExtrude","CAP_EDGE",EDGE,{"disambiguationData":[OSD([sQuery(id+"F40.wireOp",EDGE,"E348")])],"isStart":true});
            chamfer(context, id + "F45", {"entities" : qUnion([Q0, Q1]), "chamferType" : ChamferType.TWO_OFFSETS, "width1" : 10.16 * mm, "oppositeDirection" : false, "width2" : 5.08 * mm, "tangentPropagation" : true});
        }
        {
            var Q0;
            Q0=makeQuery(id+"F41.opExtrude","CAP_EDGE",EDGE,{"disambiguationData":[OSD([sQuery(id+"F40.wireOp",EDGE,"E340")])],"isStart":true});
            var Q1;
            Q1=makeQuery(id+"F41.opExtrude","CAP_EDGE",EDGE,{"disambiguationData":[OSD([sQuery(id+"F40.wireOp",EDGE,"E342")])],"isStart":true});
            var Q2;
            Q2=makeQuery(id+"F41.opExtrude","CAP_EDGE",EDGE,{"disambiguationData":[OSD([sQuery(id+"F40.wireOp",EDGE,"E341")])],"isStart":true});
            chamfer(context, id + "F46", {"entities" : qUnion([Q0, Q1, Q2]), "chamferType" : ChamferType.TWO_OFFSETS, "width1" : 7.62 * mm, "oppositeDirection" : false, "width2" : 5.08 * mm, "tangentPropagation" : true});
        }
        {
            var Q0;
            Q0=makeQuery(id+"F39.opExtrude","CAP_EDGE",EDGE,{"disambiguationData":[OSD([sQuery(id+"F38.wireOp",EDGE,"E323")])],"isStart":true});
            chamfer(context, id + "F47", {"entities" : qUnion([Q0]), "chamferType" : ChamferType.TWO_OFFSETS, "width1" : 1.27 * mm, "oppositeDirection" : false, "width2" : 30.48 * mm, "tangentPropagation" : true});
        }
        {
            var Q0;
            Q0=makeQuery(id+"F41.opExtrude","CAP_EDGE",EDGE,{"disambiguationData":[OSD([sQuery(id+"F40.wireOp",EDGE,"E350")])],"isStart":true});
            chamfer(context, id + "F48", {"entities" : qUnion([Q0]), "chamferType" : ChamferType.TWO_OFFSETS, "width1" : 15.24 * mm, "oppositeDirection" : false, "width2" : 6.35 * mm, "tangentPropagation" : true});
        }
        {
            var Q0;
            Q0=makeQuery(id+"F41.opExtrude","CAP_EDGE",EDGE,{"disambiguationData":[OSD([sQuery(id+"F40.wireOp",EDGE,"E336")])],"isStart":false});
            chamfer(context, id + "F49", {"entities" : qUnion([Q0]), "chamferType" : ChamferType.TWO_OFFSETS, "width1" : 6.35 * mm, "oppositeDirection" : false, "width2" : 15.24 * mm, "tangentPropagation" : true});
        }
        {
            var Q0;
            Q0=qCreatedBy(makeId("Top.planeOp"),FACE);
            var sketch = newSketch(context, id + "F50", { "sketchPlane" : qUnion([Q0])});
            skArc(sketch, "E352", {"start": v(410.31, 141.87) * mm, "mid": v(403.12, 138.84) * mm, "end": v(400.15, 131.63) * mm});
            skLineSegment(sketch, "E353", {"start": v(400.15, 131.63) * mm, "end": v(400.15, 122.5) * mm});
            skArc(sketch, "E354", {"start": v(398.91, 106.86) * mm, "mid": v(399.84, 114.66) * mm, "end": v(400.15, 122.5) * mm});
            skArc(sketch, "E355", {"start": v(505.72, 139.13) * mm, "mid": v(477.56, 143.25) * mm, "end": v(449.13, 142.24) * mm});
            skLineSegment(sketch, "E356", {"start": v(449.13, 142.24) * mm, "end": v(410.31, 141.87) * mm});
            skArc(sketch, "E357", {"start": v(505.72, 139.13) * mm, "mid": v(515.06, 151.96) * mm, "end": v(515.18, 167.83) * mm});
            skLineSegment(sketch, "E358", {"start": v(399.4, 110.27) * mm, "end": v(322.73, 112.1) * mm});
            skArc(sketch, "E359", {"start": v(158.85, 132.26) * mm, "mid": v(240.3, 118.13) * mm, "end": v(322.73, 112.1) * mm});
            skLineSegment(sketch, "E360", {"start": v(266.6, 150.63) * mm, "end": v(456.93, 166.14) * mm});
            skArc(sketch, "E361", {"start": v(477.05, 166.75) * mm, "mid": v(496.13, 167.03) * mm, "end": v(515.18, 167.83) * mm});
            skArc(sketch, "E362", {"start": v(477.05, 166.75) * mm, "mid": v(466.98, 166.7) * mm, "end": v(456.93, 166.14) * mm});
            skArc(sketch, "E363", {"start": v(266.6, 150.63) * mm, "mid": v(212.33, 143.8) * mm, "end": v(158.85, 132.26) * mm});
            skLineSegment(sketch, "E364", {"start": v(407.17, 141.35) * mm, "end": v(398.6, 155.03) * mm});
            skLineSegment(sketch, "E365", {"start": v(398.6, 155.03) * mm, "end": v(398.2, 161.35) * mm});
            skArc(sketch, "E366", {"start": v(401.78, 137.17) * mm, "mid": v(384.86, 153.6) * mm, "end": v(361.77, 158.39) * mm});
            skSolve(sketch);
        }
        {
            var Q0;
            Q0=qCreatedBy(makeId("Top.planeOp"),FACE);
            var sketch = newSketch(context, id + "F51", { "sketchPlane" : qUnion([Q0])});
            skArc(sketch, "E367", {"start": v(500.23, 259) * mm, "mid": v(493.04, 255.97) * mm, "end": v(490.07, 248.76) * mm});
            skLineSegment(sketch, "E368", {"start": v(490.07, 248.76) * mm, "end": v(490.07, 239.64) * mm});
            skArc(sketch, "E369", {"start": v(488.83, 223.99) * mm, "mid": v(489.76, 231.8) * mm, "end": v(490.07, 239.64) * mm});
            skArc(sketch, "E370", {"start": v(595.63, 256.26) * mm, "mid": v(567.48, 260.38) * mm, "end": v(539.05, 259.38) * mm});
            skLineSegment(sketch, "E371", {"start": v(539.05, 259.38) * mm, "end": v(500.23, 259) * mm});
            skArc(sketch, "E372", {"start": v(595.63, 256.26) * mm, "mid": v(604.98, 269.09) * mm, "end": v(605.1, 284.96) * mm});
            skLineSegment(sketch, "E373", {"start": v(489.31, 227.4) * mm, "end": v(412.65, 229.22) * mm});
            skArc(sketch, "E374", {"start": v(248.77, 249.39) * mm, "mid": v(330.21, 235.26) * mm, "end": v(412.65, 229.22) * mm});
            skLineSegment(sketch, "E375", {"start": v(356.52, 267.76) * mm, "end": v(546.85, 283.27) * mm});
            skArc(sketch, "E376", {"start": v(566.97, 283.89) * mm, "mid": v(586.04, 284.16) * mm, "end": v(605.1, 284.96) * mm});
            skArc(sketch, "E377", {"start": v(566.97, 283.89) * mm, "mid": v(556.9, 283.84) * mm, "end": v(546.85, 283.27) * mm});
            skArc(sketch, "E378", {"start": v(356.52, 267.76) * mm, "mid": v(302.25, 260.94) * mm, "end": v(248.77, 249.39) * mm});
            skLineSegment(sketch, "E379", {"start": v(497.09, 258.48) * mm, "end": v(488.52, 272.16) * mm});
            skLineSegment(sketch, "E380", {"start": v(488.52, 272.16) * mm, "end": v(488.11, 278.49) * mm});
            skArc(sketch, "E381", {"start": v(491.7, 254.3) * mm, "mid": v(474.78, 270.73) * mm, "end": v(451.69, 275.52) * mm});
            skArc(sketch, "E382", {"start": v(411.36, 383.33) * mm, "mid": v(404.17, 380.3) * mm, "end": v(401.2, 373.08) * mm});
            skLineSegment(sketch, "E383", {"start": v(401.2, 373.08) * mm, "end": v(401.2, 363.96) * mm});
            skArc(sketch, "E384", {"start": v(399.96, 348.31) * mm, "mid": v(400.88, 356.11) * mm, "end": v(401.2, 363.96) * mm});
            skArc(sketch, "E385", {"start": v(506.76, 380.58) * mm, "mid": v(478.6, 384.7) * mm, "end": v(450.17, 383.7) * mm});
            skLineSegment(sketch, "E386", {"start": v(450.17, 383.7) * mm, "end": v(411.36, 383.33) * mm});
            skArc(sketch, "E387", {"start": v(506.76, 380.58) * mm, "mid": v(516.1, 393.4) * mm, "end": v(516.23, 409.28) * mm});
            skLineSegment(sketch, "E388", {"start": v(400.44, 351.72) * mm, "end": v(323.77, 353.55) * mm});
            skArc(sketch, "E389", {"start": v(159.9, 373.7) * mm, "mid": v(241.34, 359.59) * mm, "end": v(323.77, 353.55) * mm});
            skLineSegment(sketch, "E390", {"start": v(267.65, 392.08) * mm, "end": v(457.97, 407.6) * mm});
            skArc(sketch, "E391", {"start": v(478.1, 408.2) * mm, "mid": v(497.17, 408.48) * mm, "end": v(516.23, 409.28) * mm});
            skArc(sketch, "E392", {"start": v(478.1, 408.2) * mm, "mid": v(468.03, 408.16) * mm, "end": v(457.97, 407.6) * mm});
            skArc(sketch, "E393", {"start": v(267.65, 392.08) * mm, "mid": v(213.37, 385.26) * mm, "end": v(159.9, 373.7) * mm});
            skLineSegment(sketch, "E394", {"start": v(408.21, 382.8) * mm, "end": v(399.65, 396.48) * mm});
            skLineSegment(sketch, "E395", {"start": v(399.65, 396.48) * mm, "end": v(399.24, 402.8) * mm});
            skArc(sketch, "E396", {"start": v(402.82, 378.62) * mm, "mid": v(385.9, 395.05) * mm, "end": v(362.81, 399.84) * mm});
            skSolve(sketch);
        }
        {
            var Q0;
            {var subQ1=sQuery(id+"F50.wireOp",EDGE,"E353");Q0=makeQuery(id+"F50.imprint","IMPRINT",FACE,{"disambiguationData":[TD([[makeQuery(id+"F50.imprint","IMPRINT",EDGE,{"derivedFrom":subQ1}),-1.0]])]});}
            var Q1;
            {var subQ0=sQuery(id+"F50.wireOp",EDGE,"e09726e7-f89f-41be-ab05-2f93cda8bc41");Q1=makeQuery(id+"F50.imprint","IMPRINT",FACE,{"disambiguationData":[TD([[makeQuery(id+"F50.imprint","IMPRINT",EDGE,{"derivedFrom":subQ0}),1.0]])]});}
            var Q2;
            {var subQ3=sQuery(id+"F50.wireOp",EDGE,"rTZb8FZp-XxPU-JYrP-LaRq-OZqhLN4ljL5X");Q2=makeQuery(id+"F50.imprint","IMPRINT",FACE,{"disambiguationData":[TD([[makeQuery(id+"F50.imprint","IMPRINT",EDGE,{"derivedFrom":subQ3}),-1.0]])]});}
            var Q3;
            {var subQ1=sQuery(id+"F50.wireOp",EDGE,"E364");Q3=makeQuery(id+"F50.imprint","IMPRINT",FACE,{"disambiguationData":[TD([[makeQuery(id+"F50.imprint","IMPRINT",EDGE,{"derivedFrom":subQ1}),1.0]])]});}
            var Q4;
            Q4=makeQuery(id+"F50.imprint","IMPRINT",FACE,{"disambiguationData":[TD([[makeQuery(id+"F50.imprint","IMPRINT",EDGE,{"derivedFrom":sQuery(id+"F50.wireOp",EDGE,"E355")}),-1.0]])]});
            extrude(context, id + "F52", {"entities" : qUnion([Q0, Q1, Q2, Q3, Q4]), "depth" : 2.54 * mm, "offsetDistance" : 25.4 * mm});
        }
        {
            var Q0;
            Q0=makeQuery(id+"F52.opExtrude","CAP_EDGE",EDGE,{"disambiguationData":[OSD([sQuery(id+"F50.wireOp",EDGE,"E358")])],"isStart":false});
            var Q1;
            Q1=makeQuery(id+"F52.opExtrude","CAP_EDGE",EDGE,{"disambiguationData":[OSD([sQuery(id+"F50.wireOp",EDGE,"E359")])],"isStart":false});
            chamfer(context, id + "F53", {"entities" : qUnion([Q0, Q1]), "chamferType" : ChamferType.TWO_OFFSETS, "width1" : 1.14 * mm, "oppositeDirection" : false, "width2" : 30.48 * mm, "tangentPropagation" : true});
        }
        {
            var Q0;
            Q0=makeQuery(id+"F52.opExtrude","CAP_EDGE",EDGE,{"disambiguationData":[OSD([sQuery(id+"F50.wireOp",EDGE,"E358")])],"isStart":true});
            chamfer(context, id + "F54", {"entities" : qUnion([Q0]), "chamferType" : ChamferType.TWO_OFFSETS, "width1" : 30.48 * mm, "oppositeDirection" : false, "width2" : 1.14 * mm, "tangentPropagation" : true});
        }
        {
            var Q0;
            Q0=makeQuery(id+"F51.imprint","IMPRINT",FACE,{"disambiguationData":[TD([[makeQuery(id+"F51.imprint","IMPRINT",EDGE,{"derivedFrom":sQuery(id+"F51.wireOp",EDGE,"E385")}),-1.0]])]});
            var Q1;
            Q1=makeQuery(id+"F51.imprint","IMPRINT",FACE,{"disambiguationData":[TD([[makeQuery(id+"F51.imprint","IMPRINT",EDGE,{"derivedFrom":sQuery(id+"F51.wireOp",EDGE,"E370")}),-1.0]])]});
            extrude(context, id + "F55", {"entities" : qUnion([Q0, Q1]), "depth" : 6.35 * mm, "offsetDistance" : 25.4 * mm});
        }
        {
            var Q0;
            Q0=makeQuery(id+"F55.opExtrude","CAP_EDGE",EDGE,{"disambiguationData":[OSD([sQuery(id+"F51.wireOp",EDGE,"E371")])],"isStart":false});
            var Q1;
            Q1=makeQuery(id+"F55.opExtrude","CAP_EDGE",EDGE,{"disambiguationData":[OSD([sQuery(id+"F51.wireOp",EDGE,"E370")])],"isStart":false});
            var Q2;
            Q2=makeQuery(id+"F55.opExtrude","CAP_EDGE",EDGE,{"disambiguationData":[OSD([sQuery(id+"F51.wireOp",EDGE,"E367")])],"isStart":false});
            chamfer(context, id + "F56", {"entities" : qUnion([Q0, Q1, Q2]), "chamferType" : ChamferType.TWO_OFFSETS, "width1" : 5.08 * mm, "oppositeDirection" : false, "width2" : 10.16 * mm, "tangentPropagation" : true});
        }
        {
            var Q0;
            Q0=makeQuery(id+"F55.opExtrude","CAP_EDGE",EDGE,{"disambiguationData":[OSD([sQuery(id+"F51.wireOp",EDGE,"E376")])],"isStart":false});
            var Q1;
            Q1=makeQuery(id+"F55.opExtrude","CAP_EDGE",EDGE,{"disambiguationData":[OSD([sQuery(id+"F51.wireOp",EDGE,"E375")])],"isStart":false});
            chamfer(context, id + "F57", {"entities" : qUnion([Q0, Q1]), "chamferType" : ChamferType.TWO_OFFSETS, "width1" : 5.08 * mm, "oppositeDirection" : false, "width2" : 6.35 * mm, "tangentPropagation" : true});
        }
        {
            var Q0;
            Q0=makeQuery(id+"F55.opExtrude","CAP_EDGE",EDGE,{"disambiguationData":[OSD([sQuery(id+"F51.wireOp",EDGE,"E379")])],"isStart":false});
            chamfer(context, id + "F58", {"entities" : qUnion([Q0]), "chamferType" : ChamferType.TWO_OFFSETS, "width1" : 1.02 * mm, "oppositeDirection" : false, "width2" : 127 * mm, "tangentPropagation" : true});
        }
        {
            var Q0;
            Q0=makeQuery(id+"F55.opExtrude","CAP_EDGE",EDGE,{"disambiguationData":[OSD([sQuery(id+"F51.wireOp",EDGE,"E386")])],"isStart":true});
            var Q1;
            Q1=makeQuery(id+"F55.opExtrude","CAP_EDGE",EDGE,{"disambiguationData":[OSD([sQuery(id+"F51.wireOp",EDGE,"E385")])],"isStart":true});
            chamfer(context, id + "F59", {"entities" : qUnion([Q0, Q1]), "chamferType" : ChamferType.TWO_OFFSETS, "width1" : 10.16 * mm, "oppositeDirection" : false, "width2" : 5.08 * mm, "tangentPropagation" : true});
        }
        {
            var Q0;
            Q0=makeQuery(id+"F55.opExtrude","CAP_EDGE",EDGE,{"disambiguationData":[OSD([sQuery(id+"F51.wireOp",EDGE,"E390")])],"isStart":true});
            var Q1;
            Q1=makeQuery(id+"F55.opExtrude","CAP_EDGE",EDGE,{"disambiguationData":[OSD([sQuery(id+"F51.wireOp",EDGE,"E391")])],"isStart":true});
            chamfer(context, id + "F60", {"entities" : qUnion([Q0, Q1]), "chamferType" : ChamferType.TWO_OFFSETS, "width1" : 6.35 * mm, "oppositeDirection" : false, "width2" : 5.08 * mm, "tangentPropagation" : true});
        }
        {
            var Q0;
            Q0=makeQuery(id+"F55.opExtrude","CAP_EDGE",EDGE,{"disambiguationData":[OSD([sQuery(id+"F51.wireOp",EDGE,"E394")])],"isStart":true});
            chamfer(context, id + "F61", {"entities" : qUnion([Q0]), "chamferType" : ChamferType.TWO_OFFSETS, "width1" : 127 * mm, "oppositeDirection" : false, "width2" : 1.02 * mm, "tangentPropagation" : true});
        }
        {
            var Q0;
            {var subQ0=sQuery(id+"F51.wireOp",EDGE,"E379");Q0=makeQuery(id+"F58.opChamfer","BLEND_EDGE",EDGE,{"blendedFrom":[makeQuery(id+"F55.opExtrude","CAP_EDGE",EDGE,{"disambiguationData":[OSD([subQ0])],"isStart":false}),makeQuery(id+"F55.opExtrude","SWEPT_FACE",FACE,{"disambiguationData":[OSD([subQ0])]})],"blendedInto":[makeQuery(id+"F55.opExtrude","SWEPT_FACE",FACE,{"disambiguationData":[OSD([subQ0])]})]});}
            chamfer(context, id + "F62", {"entities" : qUnion([Q0]), "chamferType" : ChamferType.TWO_OFFSETS, "width1" : 3.8 * mm, "oppositeDirection" : false, "width2" : 17.78 * mm, "tangentPropagation" : true});
        }
        {
            var Q0;
            {var subQ0=sQuery(id+"F51.wireOp",EDGE,"E394");Q0=makeQuery(id+"F61.opChamfer","BLEND_EDGE",EDGE,{"blendedFrom":[makeQuery(id+"F55.opExtrude","CAP_EDGE",EDGE,{"disambiguationData":[OSD([subQ0])],"isStart":true}),makeQuery(id+"F55.opExtrude","SWEPT_FACE",FACE,{"disambiguationData":[OSD([subQ0])]})],"blendedInto":[makeQuery(id+"F55.opExtrude","SWEPT_FACE",FACE,{"disambiguationData":[OSD([subQ0])]})]});}
            chamfer(context, id + "F63", {"entities" : qUnion([Q0]), "chamferType" : ChamferType.TWO_OFFSETS, "width1" : 3.8 * mm, "oppositeDirection" : false, "width2" : 17.78 * mm, "tangentPropagation" : true});
        }
    });
